# Revit family: 879-105X99-001-DN50-600
name_source: partatom
category: Pipe Accessories
units: mm (PartAtom-declared; Revit-internal decimal feet)

## family parameters
Always vertical = Yes
Cut with Voids When Loaded = No
Part Type = Valve - Breaks Into
Round Connector Dimension = Use Diameter
Shared = No
Work Plane-Based = No

## types (42) — shared parameters
879-0050-10-14400559999 = DN50_PN10/16
879-0050-10-144005599A0 = DN50_PN10/16
879-0065-10-14400559999 = DN65_PN10/16
879-0065-10-144005599A0 = DN65_PN10/16
879-0080-10-14400559999 = DN80_PN10/16
879-0080-10-144005599A0 = DN80_PN10/16
879-0100-10-14400559999 = DN100_PN10/16
879-0100-10-144005599A0 = DN100_PN10/16
879-0150-10-14400559999 = DN150_PN10/16
879-0150-10-144005599A0 = DN150_PN10/16
879-0200-10-04400559999 = DN200_PN10
879-0200-10-044005599A0 = DN200_PN10
879-0200-10-14400559999 = DN200_PN16
879-0200-10-144005599A0 = DN200_PN16
879-0250-10-04400559999 = DN250_PN10
879-0250-10-044005599A0 = DN250_PN10
879-0250-10-14400559999 = DN250_PN16
879-0250-10-144005599A0 = DN250_PN16
879-0300-10-04400559999 = DN300_PN10
879-0300-10-044005599A0 = DN300_PN10
879-0300-10-14400559999 = DN300_PN16
879-0300-10-144005599A0 = DN300_PN16
879-0350-10-04400559999 = DN350_PN10
879-0350-10-044005599A0 = DN350_PN10
879-0350-10-14400559999 = DN350_PN16
879-0350-10-144005599A0 = DN350_PN16
879-0400-10-04400559999 = DN400_PN10
879-0400-10-044005599A0 = DN400_PN10
879-0400-10-14400559999 = DN400_PN16
879-0400-10-144005599A0 = DN400_PN16
879-0450-10-04400559999 = DN450_PN10
879-0450-10-044005599A0 = DN450_PN10
879-0450-10-14400559999 = DN450_PN16
879-0450-10-144005599A0 = DN450_PN16
879-0500-10-04400559999 = DN500_PN10
879-0500-10-044005599A0 = DN500_PN10
879-0500-10-14400559999 = DN500_PN16
879-0500-10-144005599A0 = DN500_PN16
879-0600-10-04400559999 = DN600_PN10
879-0600-10-044005599A0 = DN600_PN10
879-0600-10-14400559999 = DN600_PN16
879-0600-10-144005599A0 = DN600_PN16
Body_wall_thickness = 10 mm  [stored 0.0328084 ft]
Description_ = AVK MODULATING FLOAT LEVEL CONTROL VALVE
Search_Table = 879-105X99-001-DN50-600
URL product pages = https://www.avkvalves.com

## per-type parameters (varying)
- 879-0050-10-14400559999_DN50_PN10/16: Body_Collar_Dia=18 mm; Body_Collar_Dia_2=12 mm  [stored 0.0393701 ft]; Body_Flange_Dia=61 mm; Body_Flange_Dia_2=64 mm; Body_Height_1=77 mm; Body_Height_2=29 mm; Body_Height_3=60 mm; Body_Height_4=44 mm; Body_Top_Dia=8 mm  [stored 0.0262467 ft]; Body_Top_Dia_2=6 mm  [stored 0.019685 ft]; Body_With_Dia=46 mm; Body_With_Dia_1=58 mm; Body_With_Dia_2=51 mm; Bolt_support=177 mm; Bolt_support_2=88 mm; Bolt_support_Dia=12 mm  [stored 0.0393701 ft]; Bolt_support_lenght=45 mm; Bolt_support_lenght_2=55 mm; Bottom_profile=13 mm  [stored 0.0426509 ft]; D1=50 mm; D3=83 mm; DN=50 mm; Fillet_Length=6 mm  [stored 0.019685 ft]; Fillet_Length_2=24 mm  [stored 0.0787402 ft]; Flange_thickness=19 mm  [stored 0.062336 ft]; H3=321 mm; H3_Ref=302 mm; H3_Ref_2=140 mm; ID=25 mm  [stored 0.082021 ft]; L=230 mm; PG_Dia=25 mm  [stored 0.082021 ft]; PG_Ref=51 mm; PG_depth=8 mm  [stored 0.0262467 ft]; PG_height=188 mm; PG_height_1=176 mm; PG_ref=35 mm  [stored 0.114829 ft]; PR_1=22 mm  [stored 0.0721785 ft]; P_lenght=33 mm  [stored 0.108268 ft]; Pilot_Dia_1=15 mm  [stored 0.0492126 ft]; Pilot_Dia_2=30 mm  [stored 0.0984252 ft]; Pilot_Dia_3=10 mm  [stored 0.0328084 ft]; Pilot_Dia_4=5 mm  [stored 0.0164042 ft]; Pilot_Dia_5=3 mm  [stored 0.00984252 ft]; Pilot_top_1=209 mm; Pilot_top_ref=19 mm  [stored 0.062336 ft]; Profile1_Height=100 mm; Profile1_Length=22 mm  [stored 0.0721785 ft]; Profile1_Length_2=15 mm  [stored 0.0492126 ft]; Profile_Dia=6 mm  [stored 0.019685 ft]; Profile_Dia_2=6 mm  [stored 0.019685 ft]; Profile_Dia_3=12 mm  [stored 0.0393701 ft]; Profile_height ref=41 mm  [stored 0.134514 ft]; T_Height=98 mm; T_Height_2=84 mm; T_Height_Ref_1=14 mm  [stored 0.0459318 ft]; T_Height_Ref_2=16 mm  [stored 0.0524934 ft]; Top_Profile=106 mm; Top_Profile_Ref=111 mm; W=237 mm; W_Ref=231 mm
- 879-0050-10-144005599A0_DN50_PN10/16: Body_Collar_Dia=18 mm; Body_Collar_Dia_2=12 mm  [stored 0.0393701 ft]; Body_Flange_Dia=61 mm; Body_Flange_Dia_2=64 mm; Body_Height_1=77 mm; Body_Height_2=29 mm; Body_Height_3=80 mm; Body_Height_4=44 mm; Body_Top_Dia=8 mm  [stored 0.0262467 ft]; Body_Top_Dia_2=6 mm  [stored 0.019685 ft]; Body_With_Dia=46 mm; Body_With_Dia_1=58 mm; Body_With_Dia_2=51 mm; Bolt_support=177 mm; Bolt_support_2=88 mm; Bolt_support_Dia=12 mm  [stored 0.0393701 ft]; Bolt_support_lenght=45 mm; Bolt_support_lenght_2=55 mm; Bottom_profile=13 mm  [stored 0.0426509 ft]; D1=50 mm; D3=83 mm; DN=50 mm; Fillet_Length=6 mm  [stored 0.019685 ft]; Fillet_Length_2=24 mm  [stored 0.0787402 ft]; Flange_thickness=19 mm  [stored 0.062336 ft]; H3=407 mm; H3_Ref=355 mm; H3_Ref_2=140 mm; ID=25 mm  [stored 0.082021 ft]; L=230 mm; PG_Dia=25 mm  [stored 0.082021 ft]; PG_Ref=51 mm; PG_depth=8 mm  [stored 0.0262467 ft]; PG_height=215 mm; PG_height_1=203 mm; PG_ref=35 mm  [stored 0.114829 ft]; PR_1=39 mm  [stored 0.127953 ft]; P_lenght=33 mm  [stored 0.108268 ft]; Pilot_Dia_1=15 mm  [stored 0.0492126 ft]; Pilot_Dia_2=30 mm  [stored 0.0984252 ft]; Pilot_Dia_3=10 mm  [stored 0.0328084 ft]; Pilot_Dia_4=5 mm  [stored 0.0164042 ft]; Pilot_Dia_5=3 mm  [stored 0.00984252 ft]; Pilot_top_1=262 mm; Pilot_top_ref=52 mm; Profile1_Height=110 mm; Profile1_Length=22 mm  [stored 0.0721785 ft]; Profile1_Length_2=15 mm  [stored 0.0492126 ft]; Profile_Dia=6 mm  [stored 0.019685 ft]; Profile_Dia_2=6 mm  [stored 0.019685 ft]; Profile_Dia_3=12 mm  [stored 0.0393701 ft]; Profile_height ref=41 mm  [stored 0.134514 ft]; T_Height=174 mm; T_Height_2=149 mm; T_Height_Ref_1=25 mm  [stored 0.082021 ft]; T_Height_Ref_2=29 mm; Top_Profile=106 mm; Top_Profile_Ref=111 mm; W=237 mm; W_Ref=231 mm
- 879-0065-10-14400559999_DN65_PN10/16: Body_Collar_Dia=22 mm  [stored 0.0721785 ft]; Body_Collar_Dia_2=15 mm  [stored 0.0492126 ft]; Body_Flange_Dia=76 mm; Body_Flange_Dia_2=81 mm; Body_Height_1=97 mm; Body_Height_2=36 mm  [stored 0.11811 ft]; Body_Height_3=58 mm; Body_Height_4=51 mm; Body_Top_Dia=10 mm  [stored 0.0328084 ft]; Body_Top_Dia_2=8 mm  [stored 0.0262467 ft]; Body_With_Dia=58 mm; Body_With_Dia_1=73 mm; Body_With_Dia_2=64 mm; Bolt_support=223 mm; Bolt_support_2=112 mm; Bolt_support_Dia=12 mm  [stored 0.0393701 ft]; Bolt_support_lenght=53 mm; Bolt_support_lenght_2=63 mm; Bottom_profile=16 mm  [stored 0.0524934 ft]; D1=59 mm; D3=93 mm; DN=65 mm; Fillet_Length=6 mm  [stored 0.019685 ft]; Fillet_Length_2=24 mm  [stored 0.0787402 ft]; Flange_thickness=19 mm  [stored 0.062336 ft]; H3=352 mm; H3_Ref=335 mm; H3_Ref_2=168 mm; ID=33 mm  [stored 0.108268 ft]; L=290 mm; PG_Dia=33 mm  [stored 0.108268 ft]; PG_Ref=64 mm; PG_depth=8 mm  [stored 0.0262467 ft]; PG_height=213 mm; PG_height_1=197 mm; PG_ref=43 mm; PR_1=23 mm  [stored 0.0754593 ft]; P_lenght=39 mm  [stored 0.127953 ft]; Pilot_Dia_1=18 mm; Pilot_Dia_2=35 mm  [stored 0.114829 ft]; Pilot_Dia_3=12 mm  [stored 0.0393701 ft]; Pilot_Dia_4=6 mm  [stored 0.019685 ft]; Pilot_Dia_5=4 mm  [stored 0.0131234 ft]; Pilot_top_1=233 mm; Pilot_top_ref=17 mm; Profile1_Height=117 mm; Profile1_Length=25 mm  [stored 0.082021 ft]; Profile1_Length_2=17 mm; Profile_Dia=6 mm  [stored 0.019685 ft]; Profile_Dia_2=6 mm  [stored 0.019685 ft]; Profile_Dia_3=12 mm  [stored 0.0393701 ft]; Profile_height ref=41 mm  [stored 0.134514 ft]; T_Height=102 mm; T_Height_2=87 mm; T_Height_Ref_1=15 mm  [stored 0.0492126 ft]; T_Height_Ref_2=17 mm; Top_Profile=134 mm; Top_Profile_Ref=139 mm; W=245 mm; W_Ref=239 mm
- 879-0065-10-144005599A0_DN65_PN10/16: Body_Collar_Dia=22 mm  [stored 0.0721785 ft]; Body_Collar_Dia_2=15 mm  [stored 0.0492126 ft]; Body_Flange_Dia=76 mm; Body_Flange_Dia_2=81 mm; Body_Height_1=97 mm; Body_Height_2=36 mm  [stored 0.11811 ft]; Body_Height_3=73 mm; Body_Height_4=51 mm; Body_Top_Dia=10 mm  [stored 0.0328084 ft]; Body_Top_Dia_2=8 mm  [stored 0.0262467 ft]; Body_With_Dia=58 mm; Body_With_Dia_1=73 mm; Body_With_Dia_2=64 mm; Bolt_support=223 mm; Bolt_support_2=112 mm; Bolt_support_Dia=12 mm  [stored 0.0393701 ft]; Bolt_support_lenght=53 mm; Bolt_support_lenght_2=63 mm; Bottom_profile=16 mm  [stored 0.0524934 ft]; D1=59 mm; D3=93 mm; DN=65 mm; Fillet_Length=6 mm  [stored 0.019685 ft]; Fillet_Length_2=24 mm  [stored 0.0787402 ft]; Flange_thickness=19 mm  [stored 0.062336 ft]; H3=436 mm; H3_Ref=384 mm; H3_Ref_2=168 mm; ID=33 mm  [stored 0.108268 ft]; L=290 mm; PG_Dia=33 mm  [stored 0.108268 ft]; PG_Ref=64 mm; PG_depth=8 mm  [stored 0.0262467 ft]; PG_height=246 mm; PG_height_1=230 mm; PG_ref=43 mm; PR_1=38 mm; P_lenght=39 mm  [stored 0.127953 ft]; Pilot_Dia_1=18 mm; Pilot_Dia_2=35 mm  [stored 0.114829 ft]; Pilot_Dia_3=12 mm  [stored 0.0393701 ft]; Pilot_Dia_4=6 mm  [stored 0.019685 ft]; Pilot_Dia_5=4 mm  [stored 0.0131234 ft]; Pilot_top_1=282 mm; Pilot_top_ref=52 mm; Profile1_Height=135 mm; Profile1_Length=25 mm  [stored 0.082021 ft]; Profile1_Length_2=17 mm; Profile_Dia=6 mm  [stored 0.019685 ft]; Profile_Dia_2=6 mm  [stored 0.019685 ft]; Profile_Dia_3=12 mm  [stored 0.0393701 ft]; Profile_height ref=41 mm  [stored 0.134514 ft]; T_Height=168 mm; T_Height_2=144 mm; T_Height_Ref_1=24 mm  [stored 0.0787402 ft]; T_Height_Ref_2=28 mm  [stored 0.0918635 ft]; Top_Profile=134 mm; Top_Profile_Ref=139 mm; W=245 mm; W_Ref=239 mm
- 879-0080-10-14400559999_DN80_PN10/16: Body_Collar_Dia=24 mm  [stored 0.0787402 ft]; Body_Collar_Dia_2=16 mm  [stored 0.0524934 ft]; Body_Flange_Dia=82 mm; Body_Flange_Dia_2=86 mm; Body_Height_1=103 mm; Body_Height_2=39 mm  [stored 0.127953 ft]; Body_Height_3=62 mm; Body_Height_4=54 mm; Body_Top_Dia=10 mm  [stored 0.0328084 ft]; Body_Top_Dia_2=9 mm  [stored 0.0295276 ft]; Body_With_Dia=62 mm; Body_With_Dia_1=78 mm; Body_With_Dia_2=69 mm; Bolt_support=238 mm; Bolt_support_2=119 mm; Bolt_support_Dia=12 mm  [stored 0.0393701 ft]; Bolt_support_lenght=60 mm; Bolt_support_lenght_2=70 mm; Bottom_profile=20 mm  [stored 0.0656168 ft]; D1=66 mm; D3=100 mm; DN=80 mm; Fillet_Length=6 mm  [stored 0.019685 ft]; Fillet_Length_2=24 mm  [stored 0.0787402 ft]; Flange_thickness=19 mm  [stored 0.062336 ft]; H3=367 mm; H3_Ref=353 mm; H3_Ref_2=177 mm; ID=40 mm  [stored 0.131234 ft]; L=310 mm; PG_Dia=40 mm  [stored 0.131234 ft]; PG_Ref=69 mm; PG_depth=8 mm  [stored 0.0262467 ft]; PG_height=244 mm; PG_height_1=224 mm; PG_ref=50 mm; PR_1=19 mm  [stored 0.062336 ft]; P_lenght=43 mm; Pilot_Dia_1=20 mm  [stored 0.0656168 ft]; Pilot_Dia_2=39 mm  [stored 0.127953 ft]; Pilot_Dia_3=13 mm  [stored 0.0426509 ft]; Pilot_Dia_4=7 mm  [stored 0.0229659 ft]; Pilot_Dia_5=4 mm  [stored 0.0131234 ft]; Pilot_top_1=243 mm; Pilot_top_ref=14 mm  [stored 0.0459318 ft]; Profile1_Height=144 mm; Profile1_Length=27 mm; Profile1_Length_2=18 mm; Profile_Dia=6 mm  [stored 0.019685 ft]; Profile_Dia_2=6 mm  [stored 0.019685 ft]; Profile_Dia_3=12 mm  [stored 0.0393701 ft]; Profile_height ref=41 mm  [stored 0.134514 ft]; T_Height=82 mm; T_Height_2=70 mm; T_Height_Ref_1=12 mm  [stored 0.0393701 ft]; T_Height_Ref_2=14 mm  [stored 0.0459318 ft]; Top_Profile=143 mm; Top_Profile_Ref=148 mm; W=260 mm; W_Ref=254 mm
- 879-0080-10-144005599A0_DN80_PN10/16: Body_Collar_Dia=24 mm  [stored 0.0787402 ft]; Body_Collar_Dia_2=16 mm  [stored 0.0524934 ft]; Body_Flange_Dia=82 mm; Body_Flange_Dia_2=86 mm; Body_Height_1=103 mm; Body_Height_2=39 mm  [stored 0.127953 ft]; Body_Height_3=100 mm; Body_Height_4=54 mm; Body_Top_Dia=10 mm  [stored 0.0328084 ft]; Body_Top_Dia_2=9 mm  [stored 0.0295276 ft]; Body_With_Dia=62 mm; Body_With_Dia_1=78 mm; Body_With_Dia_2=69 mm; Bolt_support=238 mm; Bolt_support_2=119 mm; Bolt_support_Dia=12 mm  [stored 0.0393701 ft]; Bolt_support_lenght=60 mm; Bolt_support_lenght_2=70 mm; Bottom_profile=20 mm  [stored 0.0656168 ft]; D1=66 mm; D3=100 mm; DN=80 mm; Fillet_Length=6 mm  [stored 0.019685 ft]; Fillet_Length_2=24 mm  [stored 0.0787402 ft]; Flange_thickness=19 mm  [stored 0.062336 ft]; H3=451 mm; H3_Ref=414 mm; H3_Ref_2=177 mm; ID=40 mm  [stored 0.131234 ft]; L=310 mm; PG_Dia=40 mm  [stored 0.131234 ft]; PG_Ref=69 mm; PG_depth=8 mm  [stored 0.0262467 ft]; PG_height=254 mm; PG_height_1=234 mm; PG_ref=50 mm; PR_1=40 mm  [stored 0.131234 ft]; P_lenght=43 mm; Pilot_Dia_1=20 mm  [stored 0.0656168 ft]; Pilot_Dia_2=39 mm  [stored 0.127953 ft]; Pilot_Dia_3=13 mm  [stored 0.0426509 ft]; Pilot_Dia_4=7 mm  [stored 0.0229659 ft]; Pilot_Dia_5=4 mm  [stored 0.0131234 ft]; Pilot_top_1=304 mm; Pilot_top_ref=37 mm; Profile1_Height=133 mm; Profile1_Length=27 mm; Profile1_Length_2=18 mm; Profile_Dia=6 mm  [stored 0.019685 ft]; Profile_Dia_2=6 mm  [stored 0.019685 ft]; Profile_Dia_3=12 mm  [stored 0.0393701 ft]; Profile_height ref=41 mm  [stored 0.134514 ft]; T_Height=177 mm; T_Height_2=152 mm; T_Height_Ref_1=25 mm  [stored 0.082021 ft]; T_Height_Ref_2=30 mm  [stored 0.0984252 ft]; Top_Profile=143 mm; Top_Profile_Ref=148 mm; W=260 mm; W_Ref=254 mm
- 879-0100-10-14400559999_DN100_PN10/16: Body_Collar_Dia=27 mm; Body_Collar_Dia_2=18 mm; Body_Flange_Dia=92 mm; Body_Flange_Dia_2=97 mm; Body_Height_1=117 mm; Body_Height_2=44 mm; Body_Height_3=50 mm; Body_Height_4=59 mm; Body_Top_Dia=12 mm  [stored 0.0393701 ft]; Body_Top_Dia_2=10 mm  [stored 0.0328084 ft]; Body_With_Dia=70 mm; Body_With_Dia_1=88 mm; Body_With_Dia_2=78 mm; Bolt_support=269 mm; Bolt_support_2=135 mm; Bolt_support_Dia=12 mm  [stored 0.0393701 ft]; Bolt_support_lenght=70 mm; Bolt_support_lenght_2=80 mm; Bottom_profile=25 mm  [stored 0.082021 ft]; D1=78 mm; D3=110 mm; DN=100 mm; Fillet_Length=6 mm  [stored 0.019685 ft]; Fillet_Length_2=24 mm  [stored 0.0787402 ft]; Flange_thickness=19 mm  [stored 0.062336 ft]; H3=390 mm; H3_Ref=373 mm; H3_Ref_2=195 mm; ID=50 mm; L=350 mm; PG_Dia=50 mm; PG_Ref=78 mm; PG_depth=8 mm  [stored 0.0262467 ft]; PG_height=261 mm; PG_height_1=236 mm; PG_ref=60 mm; PR_1=20 mm  [stored 0.0656168 ft]; P_lenght=48 mm; Pilot_Dia_1=22 mm  [stored 0.0721785 ft]; Pilot_Dia_2=44 mm; Pilot_Dia_3=15 mm  [stored 0.0492126 ft]; Pilot_Dia_4=7 mm  [stored 0.0229659 ft]; Pilot_Dia_5=5 mm  [stored 0.0164042 ft]; Pilot_top_1=253 mm; Pilot_top_ref=17 mm; Profile1_Height=150 mm; Profile1_Length=30 mm  [stored 0.0984252 ft]; Profile1_Length_2=20 mm  [stored 0.0656168 ft]; Profile_Dia=6 mm  [stored 0.019685 ft]; Profile_Dia_2=6 mm  [stored 0.019685 ft]; Profile_Dia_3=12 mm  [stored 0.0393701 ft]; Profile_height ref=41 mm  [stored 0.134514 ft]; T_Height=89 mm; T_Height_2=76 mm; T_Height_Ref_1=13 mm  [stored 0.0426509 ft]; T_Height_Ref_2=15 mm  [stored 0.0492126 ft]; Top_Profile=162 mm; Top_Profile_Ref=167 mm; W=280 mm; W_Ref=274 mm
- 879-0100-10-144005599A0_DN100_PN10/16: Body_Collar_Dia=27 mm; Body_Collar_Dia_2=18 mm; Body_Flange_Dia=92 mm; Body_Flange_Dia_2=97 mm; Body_Height_1=117 mm; Body_Height_2=44 mm; Body_Height_3=95 mm; Body_Height_4=59 mm; Body_Top_Dia=12 mm  [stored 0.0393701 ft]; Body_Top_Dia_2=10 mm  [stored 0.0328084 ft]; Body_With_Dia=70 mm; Body_With_Dia_1=88 mm; Body_With_Dia_2=78 mm; Bolt_support=269 mm; Bolt_support_2=135 mm; Bolt_support_Dia=12 mm  [stored 0.0393701 ft]; Bolt_support_lenght=70 mm; Bolt_support_lenght_2=80 mm; Bottom_profile=25 mm  [stored 0.082021 ft]; D1=78 mm; D3=110 mm; DN=100 mm; Fillet_Length=6 mm  [stored 0.019685 ft]; Fillet_Length_2=24 mm  [stored 0.0787402 ft]; Flange_thickness=19 mm  [stored 0.062336 ft]; H3=474 mm; H3_Ref=437 mm; H3_Ref_2=195 mm; ID=50 mm; L=350 mm; PG_Dia=50 mm; PG_Ref=78 mm; PG_depth=8 mm  [stored 0.0262467 ft]; PG_height=273 mm; PG_height_1=248 mm; PG_ref=60 mm; PR_1=41 mm  [stored 0.134514 ft]; P_lenght=48 mm; Pilot_Dia_1=22 mm  [stored 0.0721785 ft]; Pilot_Dia_2=44 mm; Pilot_Dia_3=15 mm  [stored 0.0492126 ft]; Pilot_Dia_4=7 mm  [stored 0.0229659 ft]; Pilot_Dia_5=5 mm  [stored 0.0164042 ft]; Pilot_top_1=317 mm; Pilot_top_ref=37 mm; Profile1_Height=141 mm; Profile1_Length=30 mm  [stored 0.0984252 ft]; Profile1_Length_2=20 mm  [stored 0.0656168 ft]; Profile_Dia=6 mm  [stored 0.019685 ft]; Profile_Dia_2=6 mm  [stored 0.019685 ft]; Profile_Dia_3=12 mm  [stored 0.0393701 ft]; Profile_height ref=41 mm  [stored 0.134514 ft]; T_Height=182 mm; T_Height_2=156 mm; T_Height_Ref_1=26 mm; T_Height_Ref_2=30 mm  [stored 0.0984252 ft]; Top_Profile=162 mm; Top_Profile_Ref=167 mm; W=280 mm; W_Ref=274 mm
- 879-0150-10-14400559999_DN150_PN10/16: Body_Collar_Dia=37 mm; Body_Collar_Dia_2=24 mm  [stored 0.0787402 ft]; Body_Flange_Dia=126 mm; Body_Flange_Dia_2=133 mm; Body_Height_1=160 mm; Body_Height_2=60 mm; Body_Height_3=60 mm; Body_Height_4=75 mm; Body_Top_Dia=16 mm  [stored 0.0524934 ft]; Body_Top_Dia_2=13 mm  [stored 0.0426509 ft]; Body_With_Dia=96 mm; Body_With_Dia_1=120 mm; Body_With_Dia_2=107 mm; Bolt_support=369 mm; Bolt_support_2=185 mm; Bolt_support_Dia=16 mm  [stored 0.0524934 ft]; Bolt_support_lenght=95 mm; Bolt_support_lenght_2=105 mm; Bottom_profile=38 mm; D1=106 mm; D3=143 mm; DN=150 mm; Fillet_Length=8 mm  [stored 0.0262467 ft]; Fillet_Length_2=32 mm  [stored 0.104987 ft]; Flange_thickness=19 mm  [stored 0.062336 ft]; H3=523 mm; H3_Ref=490 mm; H3_Ref_2=255 mm; ID=75 mm; L=480 mm; PG_Dia=50 mm; PG_Ref=107 mm; PG_depth=11 mm; PG_height=320 mm; PG_height_1=295 mm; PG_ref=85 mm; PR_1=32 mm  [stored 0.104987 ft]; P_lenght=68 mm; Pilot_Dia_1=31 mm  [stored 0.101706 ft]; Pilot_Dia_2=62 mm; Pilot_Dia_3=21 mm  [stored 0.0688976 ft]; Pilot_Dia_4=10 mm  [stored 0.0328084 ft]; Pilot_Dia_5=7 mm  [stored 0.0229659 ft]; Pilot_top_1=338 mm; Pilot_top_ref=33 mm  [stored 0.108268 ft]; Profile1_Height=195 mm; Profile1_Length=39 mm  [stored 0.127953 ft]; Profile1_Length_2=26 mm; Profile_Dia=8 mm  [stored 0.0262467 ft]; Profile_Dia_2=8 mm  [stored 0.0262467 ft]; Profile_Dia_3=16 mm  [stored 0.0524934 ft]; Profile_height ref=43 mm; T_Height=143 mm; T_Height_2=122 mm; T_Height_Ref_1=20 mm  [stored 0.0656168 ft]; T_Height_Ref_2=24 mm  [stored 0.0787402 ft]; Top_Profile=222 mm; Top_Profile_Ref=227 mm; W=410 mm; W_Ref=402 mm
- 879-0150-10-144005599A0_DN150_PN10/16: Body_Collar_Dia=37 mm; Body_Collar_Dia_2=24 mm  [stored 0.0787402 ft]; Body_Flange_Dia=126 mm; Body_Flange_Dia_2=133 mm; Body_Height_1=160 mm; Body_Height_2=60 mm; Body_Height_3=115 mm; Body_Height_4=75 mm; Body_Top_Dia=16 mm  [stored 0.0524934 ft]; Body_Top_Dia_2=13 mm  [stored 0.0426509 ft]; Body_With_Dia=96 mm; Body_With_Dia_1=120 mm; Body_With_Dia_2=107 mm; Bolt_support=369 mm; Bolt_support_2=185 mm; Bolt_support_Dia=16 mm  [stored 0.0524934 ft]; Bolt_support_lenght=95 mm; Bolt_support_lenght_2=105 mm; Bottom_profile=38 mm; D1=106 mm; D3=143 mm; DN=150 mm; Fillet_Length=8 mm  [stored 0.0262467 ft]; Fillet_Length_2=32 mm  [stored 0.104987 ft]; Flange_thickness=19 mm  [stored 0.062336 ft]; H3=607 mm; H3_Ref=560 mm; H3_Ref_2=255 mm; ID=75 mm; L=480 mm; PG_Dia=50 mm; PG_Ref=107 mm; PG_depth=11 mm; PG_height=339 mm; PG_height_1=314 mm; PG_ref=85 mm; PR_1=51 mm; P_lenght=68 mm; Pilot_Dia_1=31 mm  [stored 0.101706 ft]; Pilot_Dia_2=62 mm; Pilot_Dia_3=21 mm  [stored 0.0688976 ft]; Pilot_Dia_4=10 mm  [stored 0.0328084 ft]; Pilot_Dia_5=7 mm  [stored 0.0229659 ft]; Pilot_top_1=407 mm; Pilot_top_ref=47 mm; Profile1_Height=195 mm; Profile1_Length=39 mm  [stored 0.127953 ft]; Profile1_Length_2=26 mm; Profile_Dia=8 mm  [stored 0.0262467 ft]; Profile_Dia_2=8 mm  [stored 0.0262467 ft]; Profile_Dia_3=16 mm  [stored 0.0524934 ft]; Profile_height ref=43 mm; T_Height=227 mm; T_Height_2=194 mm; T_Height_Ref_1=32 mm  [stored 0.104987 ft]; T_Height_Ref_2=38 mm; Top_Profile=222 mm; Top_Profile_Ref=227 mm; W=410 mm; W_Ref=402 mm
- 879-0200-10-04400559999_DN200_PN10: Body_Collar_Dia=46 mm; Body_Collar_Dia_2=30 mm  [stored 0.0984252 ft]; Body_Flange_Dia=158 mm; Body_Flange_Dia_2=167 mm; Body_Height_1=200 mm; Body_Height_2=75 mm; Body_Height_3=100 mm; Body_Height_4=90 mm; Body_Top_Dia=20 mm  [stored 0.0656168 ft]; Body_Top_Dia_2=17 mm; Body_With_Dia=120 mm; Body_With_Dia_1=150 mm; Body_With_Dia_2=133 mm; Bolt_support=462 mm; Bolt_support_2=231 mm; Bolt_support_Dia=20 mm  [stored 0.0656168 ft]; Bolt_support_lenght=120 mm; Bolt_support_lenght_2=130 mm; Bottom_profile=50 mm; D1=133 mm; D3=170 mm; DN=200 mm; Fillet_Length=10 mm  [stored 0.0328084 ft]; Fillet_Length_2=40 mm  [stored 0.131234 ft]; Flange_thickness=20 mm  [stored 0.0656168 ft]; H3=677 mm; H3_Ref=629 mm; H3_Ref_2=310 mm; ID=100 mm; L=600 mm; PG_Dia=67 mm; PG_Ref=133 mm; PG_depth=14 mm  [stored 0.0459318 ft]; PG_height=400 mm; PG_height_1=367 mm; PG_ref=110 mm; PR_1=51 mm; P_lenght=85 mm; Pilot_Dia_1=39 mm  [stored 0.127953 ft]; Pilot_Dia_2=77 mm; Pilot_Dia_3=26 mm; Pilot_Dia_4=13 mm  [stored 0.0426509 ft]; Pilot_Dia_5=9 mm  [stored 0.0295276 ft]; Pilot_top_1=449 mm; Pilot_top_ref=49 mm; Profile1_Height=238 mm; Profile1_Length=46 mm; Profile1_Length_2=31 mm  [stored 0.101706 ft]; Profile_Dia=10 mm  [stored 0.0328084 ft]; Profile_Dia_2=10 mm  [stored 0.0328084 ft]; Profile_Dia_3=20 mm  [stored 0.0656168 ft]; Profile_height ref=45 mm; T_Height=224 mm; T_Height_2=192 mm; T_Height_Ref_1=32 mm  [stored 0.104987 ft]; T_Height_Ref_2=37 mm; Top_Profile=277 mm; Top_Profile_Ref=282 mm; W=510 mm; W_Ref=500 mm
- 879-0200-10-044005599A0_DN200_PN10: Body_Collar_Dia=46 mm; Body_Collar_Dia_2=30 mm  [stored 0.0984252 ft]; Body_Flange_Dia=158 mm; Body_Flange_Dia_2=167 mm; Body_Height_1=200 mm; Body_Height_2=75 mm; Body_Height_3=170 mm; Body_Height_4=90 mm; Body_Top_Dia=20 mm  [stored 0.0656168 ft]; Body_Top_Dia_2=17 mm; Body_With_Dia=120 mm; Body_With_Dia_1=150 mm; Body_With_Dia_2=133 mm; Bolt_support=462 mm; Bolt_support_2=231 mm; Bolt_support_Dia=20 mm  [stored 0.0656168 ft]; Bolt_support_lenght=120 mm; Bolt_support_lenght_2=130 mm; Bottom_profile=50 mm; D1=133 mm; D3=170 mm; DN=200 mm; Fillet_Length=10 mm  [stored 0.0328084 ft]; Fillet_Length_2=40 mm  [stored 0.131234 ft]; Flange_thickness=20 mm  [stored 0.0656168 ft]; H3=774 mm; H3_Ref=712 mm; H3_Ref_2=310 mm; ID=100 mm; L=600 mm; PG_Dia=67 mm; PG_Ref=133 mm; PG_depth=14 mm  [stored 0.0459318 ft]; PG_height=424 mm; PG_height_1=391 mm; PG_ref=110 mm; PR_1=72 mm; P_lenght=85 mm; Pilot_Dia_1=39 mm  [stored 0.127953 ft]; Pilot_Dia_2=77 mm; Pilot_Dia_3=26 mm; Pilot_Dia_4=13 mm  [stored 0.0426509 ft]; Pilot_Dia_5=9 mm  [stored 0.0295276 ft]; Pilot_top_1=532 mm; Pilot_top_ref=62 mm; Profile1_Height=240 mm; Profile1_Length=46 mm; Profile1_Length_2=31 mm  [stored 0.101706 ft]; Profile_Dia=10 mm  [stored 0.0328084 ft]; Profile_Dia_2=10 mm  [stored 0.0328084 ft]; Profile_Dia_3=20 mm  [stored 0.0656168 ft]; Profile_height ref=45 mm; T_Height=319 mm; T_Height_2=273 mm; T_Height_Ref_1=46 mm; T_Height_Ref_2=53 mm; Top_Profile=277 mm; Top_Profile_Ref=282 mm; W=510 mm; W_Ref=500 mm
- 879-0200-10-14400559999_DN200_PN16: Body_Collar_Dia=46 mm; Body_Collar_Dia_2=30 mm  [stored 0.0984252 ft]; Body_Flange_Dia=158 mm; Body_Flange_Dia_2=167 mm; Body_Height_1=200 mm; Body_Height_2=75 mm; Body_Height_3=100 mm; Body_Height_4=90 mm; Body_Top_Dia=20 mm  [stored 0.0656168 ft]; Body_Top_Dia_2=17 mm; Body_With_Dia=120 mm; Body_With_Dia_1=150 mm; Body_With_Dia_2=133 mm; Bolt_support=462 mm; Bolt_support_2=231 mm; Bolt_support_Dia=20 mm  [stored 0.0656168 ft]; Bolt_support_lenght=120 mm; Bolt_support_lenght_2=130 mm; Bottom_profile=50 mm; D1=133 mm; D3=170 mm; DN=200 mm; Fillet_Length=10 mm  [stored 0.0328084 ft]; Fillet_Length_2=40 mm  [stored 0.131234 ft]; Flange_thickness=20 mm  [stored 0.0656168 ft]; H3=677 mm; H3_Ref=629 mm; H3_Ref_2=310 mm; ID=100 mm; L=600 mm; PG_Dia=67 mm; PG_Ref=133 mm; PG_depth=14 mm  [stored 0.0459318 ft]; PG_height=400 mm; PG_height_1=367 mm; PG_ref=110 mm; PR_1=51 mm; P_lenght=85 mm; Pilot_Dia_1=39 mm  [stored 0.127953 ft]; Pilot_Dia_2=77 mm; Pilot_Dia_3=26 mm; Pilot_Dia_4=13 mm  [stored 0.0426509 ft]; Pilot_Dia_5=9 mm  [stored 0.0295276 ft]; Pilot_top_1=449 mm; Pilot_top_ref=49 mm; Profile1_Height=238 mm; Profile1_Length=46 mm; Profile1_Length_2=31 mm  [stored 0.101706 ft]; Profile_Dia=10 mm  [stored 0.0328084 ft]; Profile_Dia_2=10 mm  [stored 0.0328084 ft]; Profile_Dia_3=20 mm  [stored 0.0656168 ft]; Profile_height ref=45 mm; T_Height=224 mm; T_Height_2=192 mm; T_Height_Ref_1=32 mm  [stored 0.104987 ft]; T_Height_Ref_2=37 mm; Top_Profile=277 mm; Top_Profile_Ref=282 mm; W=510 mm; W_Ref=500 mm
- 879-0200-10-144005599A0_DN200_PN16: Body_Collar_Dia=46 mm; Body_Collar_Dia_2=30 mm  [stored 0.0984252 ft]; Body_Flange_Dia=158 mm; Body_Flange_Dia_2=167 mm; Body_Height_1=200 mm; Body_Height_2=75 mm; Body_Height_3=165 mm; Body_Height_4=90 mm; Body_Top_Dia=20 mm  [stored 0.0656168 ft]; Body_Top_Dia_2=17 mm; Body_With_Dia=120 mm; Body_With_Dia_1=150 mm; Body_With_Dia_2=133 mm; Bolt_support=462 mm; Bolt_support_2=231 mm; Bolt_support_Dia=20 mm  [stored 0.0656168 ft]; Bolt_support_lenght=120 mm; Bolt_support_lenght_2=130 mm; Bottom_profile=50 mm; D1=133 mm; D3=170 mm; DN=200 mm; Fillet_Length=10 mm  [stored 0.0328084 ft]; Fillet_Length_2=40 mm  [stored 0.131234 ft]; Flange_thickness=20 mm  [stored 0.0656168 ft]; H3=774 mm; H3_Ref=710 mm; H3_Ref_2=310 mm; ID=100 mm; L=600 mm; PG_Dia=67 mm; PG_Ref=133 mm; PG_depth=14 mm  [stored 0.0459318 ft]; PG_height=424 mm; PG_height_1=391 mm; PG_ref=110 mm; PR_1=72 mm; P_lenght=85 mm; Pilot_Dia_1=39 mm  [stored 0.127953 ft]; Pilot_Dia_2=77 mm; Pilot_Dia_3=26 mm; Pilot_Dia_4=13 mm  [stored 0.0426509 ft]; Pilot_Dia_5=9 mm  [stored 0.0295276 ft]; Pilot_top_1=530 mm; Pilot_top_ref=65 mm; Profile1_Height=240 mm; Profile1_Length=46 mm; Profile1_Length_2=31 mm  [stored 0.101706 ft]; Profile_Dia=10 mm  [stored 0.0328084 ft]; Profile_Dia_2=10 mm  [stored 0.0328084 ft]; Profile_Dia_3=20 mm  [stored 0.0656168 ft]; Profile_height ref=45 mm; T_Height=319 mm; T_Height_2=273 mm; T_Height_Ref_1=46 mm; T_Height_Ref_2=53 mm; Top_Profile=277 mm; Top_Profile_Ref=282 mm; W=510 mm; W_Ref=500 mm
- 879-0250-10-04400559999_DN250_PN10: Body_Collar_Dia=56 mm; Body_Collar_Dia_2=37 mm; Body_Flange_Dia=192 mm; Body_Flange_Dia_2=203 mm; Body_Height_1=243 mm; Body_Height_2=91 mm; Body_Height_3=81 mm; Body_Height_4=106 mm; Body_Top_Dia=24 mm  [stored 0.0787402 ft]; Body_Top_Dia_2=20 mm  [stored 0.0656168 ft]; Body_With_Dia=146 mm; Body_With_Dia_1=183 mm; Body_With_Dia_2=162 mm; Bolt_support=562 mm; Bolt_support_2=281 mm; Bolt_support_Dia=20 mm  [stored 0.0656168 ft]; Bolt_support_lenght=145 mm; Bolt_support_lenght_2=155 mm; Bottom_profile=63 mm; D1=160 mm; D3=198 mm; DN=250 mm; Fillet_Length=10 mm  [stored 0.0328084 ft]; Fillet_Length_2=40 mm  [stored 0.131234 ft]; Flange_thickness=22 mm  [stored 0.0721785 ft]; H3=757 mm; H3_Ref=703 mm; H3_Ref_2=370 mm; ID=125 mm; L=730 mm; PG_Dia=83 mm; PG_Ref=162 mm; PG_depth=14 mm  [stored 0.0459318 ft]; PG_height=458 mm; PG_height_1=416 mm; PG_ref=135 mm; PR_1=54 mm; P_lenght=101 mm; Pilot_Dia_1=46 mm; Pilot_Dia_2=92 mm; Pilot_Dia_3=31 mm  [stored 0.101706 ft]; Pilot_Dia_4=15 mm  [stored 0.0492126 ft]; Pilot_Dia_5=10 mm  [stored 0.0328084 ft]; Pilot_top_1=495 mm; Pilot_top_ref=54 mm; Profile1_Height=275 mm; Profile1_Length=53 mm; Profile1_Length_2=36 mm  [stored 0.11811 ft]; Profile_Dia=10 mm  [stored 0.0328084 ft]; Profile_Dia_2=10 mm  [stored 0.0328084 ft]; Profile_Dia_3=20 mm  [stored 0.0656168 ft]; Profile_height ref=45 mm; T_Height=240 mm; T_Height_2=205 mm; T_Height_Ref_1=34 mm; T_Height_Ref_2=40 mm  [stored 0.131234 ft]; Top_Profile=337 mm; Top_Profile_Ref=342 mm; W=555 mm; W_Ref=545 mm
- 879-0250-10-044005599A0_DN250_PN10: Body_Collar_Dia=56 mm; Body_Collar_Dia_2=37 mm; Body_Flange_Dia=192 mm; Body_Flange_Dia_2=203 mm; Body_Height_1=243 mm; Body_Height_2=91 mm; Body_Height_3=160 mm; Body_Height_4=106 mm; Body_Top_Dia=24 mm  [stored 0.0787402 ft]; Body_Top_Dia_2=20 mm  [stored 0.0656168 ft]; Body_With_Dia=146 mm; Body_With_Dia_1=183 mm; Body_With_Dia_2=162 mm; Bolt_support=562 mm; Bolt_support_2=281 mm; Bolt_support_Dia=20 mm  [stored 0.0656168 ft]; Bolt_support_lenght=145 mm; Bolt_support_lenght_2=155 mm; Bottom_profile=63 mm; D1=160 mm; D3=198 mm; DN=250 mm; Fillet_Length=10 mm  [stored 0.0328084 ft]; Fillet_Length_2=40 mm  [stored 0.131234 ft]; Flange_thickness=22 mm  [stored 0.0721785 ft]; H3=854 mm; H3_Ref=791 mm; H3_Ref_2=370 mm; ID=125 mm; L=730 mm; PG_Dia=83 mm; PG_Ref=162 mm; PG_depth=14 mm  [stored 0.0459318 ft]; PG_height=495 mm; PG_height_1=453 mm; PG_ref=135 mm; PR_1=72 mm; P_lenght=101 mm; Pilot_Dia_1=46 mm; Pilot_Dia_2=92 mm; Pilot_Dia_3=31 mm  [stored 0.101706 ft]; Pilot_Dia_4=15 mm  [stored 0.0492126 ft]; Pilot_Dia_5=10 mm  [stored 0.0328084 ft]; Pilot_top_1=583 mm; Pilot_top_ref=63 mm; Profile1_Height=295 mm; Profile1_Length=53 mm; Profile1_Length_2=36 mm  [stored 0.11811 ft]; Profile_Dia=10 mm  [stored 0.0328084 ft]; Profile_Dia_2=10 mm  [stored 0.0328084 ft]; Profile_Dia_3=20 mm  [stored 0.0656168 ft]; Profile_height ref=45 mm; T_Height=317 mm; T_Height_2=271 mm; T_Height_Ref_1=45 mm; T_Height_Ref_2=53 mm; Top_Profile=337 mm; Top_Profile_Ref=342 mm; W=555 mm; W_Ref=545 mm
- 879-0250-10-14400559999_DN250_PN16: Body_Collar_Dia=56 mm; Body_Collar_Dia_2=37 mm; Body_Flange_Dia=192 mm; Body_Flange_Dia_2=203 mm; Body_Height_1=243 mm; Body_Height_2=91 mm; Body_Height_3=81 mm; Body_Height_4=106 mm; Body_Top_Dia=24 mm  [stored 0.0787402 ft]; Body_Top_Dia_2=20 mm  [stored 0.0656168 ft]; Body_With_Dia=146 mm; Body_With_Dia_1=183 mm; Body_With_Dia_2=162 mm; Bolt_support=562 mm; Bolt_support_2=281 mm; Bolt_support_Dia=20 mm  [stored 0.0656168 ft]; Bolt_support_lenght=145 mm; Bolt_support_lenght_2=155 mm; Bottom_profile=63 mm; D1=160 mm; D3=203 mm; DN=250 mm; Fillet_Length=10 mm  [stored 0.0328084 ft]; Fillet_Length_2=40 mm  [stored 0.131234 ft]; Flange_thickness=22 mm  [stored 0.0721785 ft]; H3=757 mm; H3_Ref=705 mm; H3_Ref_2=370 mm; ID=125 mm; L=730 mm; PG_Dia=83 mm; PG_Ref=162 mm; PG_depth=14 mm  [stored 0.0459318 ft]; PG_height=449 mm; PG_height_1=407 mm; PG_ref=135 mm; PR_1=55 mm; P_lenght=103 mm; Pilot_Dia_1=47 mm; Pilot_Dia_2=94 mm; Pilot_Dia_3=31 mm  [stored 0.101706 ft]; Pilot_Dia_4=16 mm  [stored 0.0524934 ft]; Pilot_Dia_5=10 mm  [stored 0.0328084 ft]; Pilot_top_1=493 mm; Pilot_top_ref=52 mm; Profile1_Height=265 mm; Profile1_Length=55 mm; Profile1_Length_2=36 mm  [stored 0.11811 ft]; Profile_Dia=10 mm  [stored 0.0328084 ft]; Profile_Dia_2=10 mm  [stored 0.0328084 ft]; Profile_Dia_3=20 mm  [stored 0.0656168 ft]; Profile_height ref=45 mm; T_Height=245 mm; T_Height_2=210 mm; T_Height_Ref_1=35 mm  [stored 0.114829 ft]; T_Height_Ref_2=41 mm  [stored 0.134514 ft]; Top_Profile=337 mm; Top_Profile_Ref=342 mm; W=555 mm; W_Ref=545 mm
- 879-0250-10-144005599A0_DN250_PN16: Body_Collar_Dia=56 mm; Body_Collar_Dia_2=37 mm; Body_Flange_Dia=192 mm; Body_Flange_Dia_2=203 mm; Body_Height_1=243 mm; Body_Height_2=91 mm; Body_Height_3=155 mm; Body_Height_4=106 mm; Body_Top_Dia=24 mm  [stored 0.0787402 ft]; Body_Top_Dia_2=20 mm  [stored 0.0656168 ft]; Body_With_Dia=146 mm; Body_With_Dia_1=183 mm; Body_With_Dia_2=162 mm; Bolt_support=562 mm; Bolt_support_2=281 mm; Bolt_support_Dia=20 mm  [stored 0.0656168 ft]; Bolt_support_lenght=145 mm; Bolt_support_lenght_2=155 mm; Bottom_profile=63 mm; D1=160 mm; D3=203 mm; DN=250 mm; Fillet_Length=10 mm  [stored 0.0328084 ft]; Fillet_Length_2=40 mm  [stored 0.131234 ft]; Flange_thickness=22 mm  [stored 0.0721785 ft]; H3=854 mm; H3_Ref=791 mm; H3_Ref_2=370 mm; ID=125 mm; L=730 mm; PG_Dia=83 mm; PG_Ref=162 mm; PG_depth=14 mm  [stored 0.0459318 ft]; PG_height=478 mm; PG_height_1=437 mm; PG_ref=135 mm; PR_1=75 mm; P_lenght=103 mm; Pilot_Dia_1=47 mm; Pilot_Dia_2=94 mm; Pilot_Dia_3=31 mm  [stored 0.101706 ft]; Pilot_Dia_4=16 mm  [stored 0.0524934 ft]; Pilot_Dia_5=10 mm  [stored 0.0328084 ft]; Pilot_top_1=578 mm; Pilot_top_ref=63 mm; Profile1_Height=275 mm; Profile1_Length=55 mm; Profile1_Length_2=36 mm  [stored 0.11811 ft]; Profile_Dia=10 mm  [stored 0.0328084 ft]; Profile_Dia_2=10 mm  [stored 0.0328084 ft]; Profile_Dia_3=20 mm  [stored 0.0656168 ft]; Profile_height ref=45 mm; T_Height=332 mm; T_Height_2=284 mm; T_Height_Ref_1=47 mm; T_Height_Ref_2=55 mm; Top_Profile=337 mm; Top_Profile_Ref=342 mm; W=555 mm; W_Ref=545 mm
- 879-0300-10-04400559999_DN300_PN10: Body_Collar_Dia=65 mm; Body_Collar_Dia_2=43 mm; Body_Flange_Dia=224 mm; Body_Flange_Dia_2=236 mm; Body_Height_1=283 mm; Body_Height_2=106 mm; Body_Height_3=95 mm; Body_Height_4=121 mm; Body_Top_Dia=28 mm  [stored 0.0918635 ft]; Body_Top_Dia_2=24 mm  [stored 0.0787402 ft]; Body_With_Dia=170 mm; Body_With_Dia_1=213 mm; Body_With_Dia_2=189 mm; Bolt_support=654 mm; Bolt_support_2=327 mm; Bolt_support_Dia=20 mm  [stored 0.0656168 ft]; Bolt_support_lenght=170 mm; Bolt_support_lenght_2=180 mm; Bottom_profile=75 mm; D1=185 mm; D3=223 mm; DN=300 mm; Fillet_Length=10 mm  [stored 0.0328084 ft]; Fillet_Length_2=40 mm  [stored 0.131234 ft]; Flange_thickness=25 mm  [stored 0.082021 ft]; H3=826 mm; H3_Ref=784 mm; H3_Ref_2=425 mm; ID=150 mm; L=850 mm; PG_Dia=100 mm; PG_Ref=189 mm; PG_depth=14 mm  [stored 0.0459318 ft]; PG_height=523 mm; PG_height_1=473 mm; PG_ref=160 mm; PR_1=53 mm; P_lenght=116 mm; Pilot_Dia_1=53 mm; Pilot_Dia_2=105 mm; Pilot_Dia_3=35 mm  [stored 0.114829 ft]; Pilot_Dia_4=18 mm; Pilot_Dia_5=12 mm  [stored 0.0393701 ft]; Pilot_top_1=551 mm; Pilot_top_ref=42 mm  [stored 0.137795 ft]; Profile1_Height=325 mm; Profile1_Length=60 mm; Profile1_Length_2=40 mm  [stored 0.131234 ft]; Profile_Dia=10 mm  [stored 0.0328084 ft]; Profile_Dia_2=10 mm  [stored 0.0328084 ft]; Profile_Dia_3=20 mm  [stored 0.0656168 ft]; Profile_height ref=45 mm; T_Height=234 mm; T_Height_2=200 mm; T_Height_Ref_1=33 mm  [stored 0.108268 ft]; T_Height_Ref_2=39 mm  [stored 0.127953 ft]; Top_Profile=392 mm; Top_Profile_Ref=397 mm; W=605 mm; W_Ref=595 mm
- 879-0300-10-044005599A0_DN300_PN10: Body_Collar_Dia=65 mm; Body_Collar_Dia_2=43 mm; Body_Flange_Dia=224 mm; Body_Flange_Dia_2=236 mm; Body_Height_1=283 mm; Body_Height_2=106 mm; Body_Height_3=140 mm; Body_Height_4=121 mm; Body_Top_Dia=28 mm  [stored 0.0918635 ft]; Body_Top_Dia_2=24 mm  [stored 0.0787402 ft]; Body_With_Dia=170 mm; Body_With_Dia_1=213 mm; Body_With_Dia_2=189 mm; Bolt_support=654 mm; Bolt_support_2=327 mm; Bolt_support_Dia=20 mm  [stored 0.0656168 ft]; Bolt_support_lenght=170 mm; Bolt_support_lenght_2=180 mm; Bottom_profile=75 mm; D1=185 mm; D3=223 mm; DN=300 mm; Fillet_Length=10 mm  [stored 0.0328084 ft]; Fillet_Length_2=40 mm  [stored 0.131234 ft]; Flange_thickness=25 mm  [stored 0.082021 ft]; H3=923 mm; H3_Ref=855 mm; H3_Ref_2=425 mm; ID=150 mm; L=850 mm; PG_Dia=100 mm; PG_Ref=189 mm; PG_depth=14 mm  [stored 0.0459318 ft]; PG_height=553 mm; PG_height_1=503 mm; PG_ref=160 mm; PR_1=72 mm; P_lenght=116 mm; Pilot_Dia_1=53 mm; Pilot_Dia_2=105 mm; Pilot_Dia_3=35 mm  [stored 0.114829 ft]; Pilot_Dia_4=18 mm; Pilot_Dia_5=12 mm  [stored 0.0393701 ft]; Pilot_top_1=623 mm; Pilot_top_ref=68 mm; Profile1_Height=335 mm; Profile1_Length=60 mm; Profile1_Length_2=40 mm  [stored 0.131234 ft]; Profile_Dia=10 mm  [stored 0.0328084 ft]; Profile_Dia_2=10 mm  [stored 0.0328084 ft]; Profile_Dia_3=20 mm  [stored 0.0656168 ft]; Profile_height ref=45 mm; T_Height=321 mm; T_Height_2=275 mm; T_Height_Ref_1=46 mm; T_Height_Ref_2=53 mm; Top_Profile=392 mm; Top_Profile_Ref=397 mm; W=605 mm; W_Ref=595 mm
- 879-0300-10-14400559999_DN300_PN16: Body_Collar_Dia=65 mm; Body_Collar_Dia_2=43 mm; Body_Flange_Dia=224 mm; Body_Flange_Dia_2=236 mm; Body_Height_1=283 mm; Body_Height_2=106 mm; Body_Height_3=95 mm; Body_Height_4=121 mm; Body_Top_Dia=28 mm  [stored 0.0918635 ft]; Body_Top_Dia_2=24 mm  [stored 0.0787402 ft]; Body_With_Dia=170 mm; Body_With_Dia_1=213 mm; Body_With_Dia_2=189 mm; Bolt_support=654 mm; Bolt_support_2=327 mm; Bolt_support_Dia=20 mm  [stored 0.0656168 ft]; Bolt_support_lenght=170 mm; Bolt_support_lenght_2=180 mm; Bottom_profile=75 mm; D1=185 mm; D3=230 mm; DN=300 mm; Fillet_Length=10 mm  [stored 0.0328084 ft]; Fillet_Length_2=40 mm  [stored 0.131234 ft]; Flange_thickness=25 mm  [stored 0.082021 ft]; H3=826 mm; H3_Ref=788 mm; H3_Ref_2=425 mm; ID=150 mm; L=850 mm; PG_Dia=100 mm; PG_Ref=189 mm; PG_depth=14 mm  [stored 0.0459318 ft]; PG_height=521 mm; PG_height_1=471 mm; PG_ref=160 mm; PR_1=51 mm; P_lenght=120 mm; Pilot_Dia_1=55 mm; Pilot_Dia_2=109 mm; Pilot_Dia_3=36 mm  [stored 0.11811 ft]; Pilot_Dia_4=18 mm; Pilot_Dia_5=12 mm  [stored 0.0393701 ft]; Pilot_top_1=548 mm; Pilot_top_ref=38 mm; Profile1_Height=325 mm; Profile1_Length=62 mm; Profile1_Length_2=41 mm  [stored 0.134514 ft]; Profile_Dia=10 mm  [stored 0.0328084 ft]; Profile_Dia_2=10 mm  [stored 0.0328084 ft]; Profile_Dia_3=20 mm  [stored 0.0656168 ft]; Profile_height ref=45 mm; T_Height=226 mm; T_Height_2=194 mm; T_Height_Ref_1=32 mm  [stored 0.104987 ft]; T_Height_Ref_2=38 mm; Top_Profile=392 mm; Top_Profile_Ref=397 mm; W=605 mm; W_Ref=595 mm
- 879-0300-10-144005599A0_DN300_PN16: Body_Collar_Dia=65 mm; Body_Collar_Dia_2=43 mm; Body_Flange_Dia=224 mm; Body_Flange_Dia_2=236 mm; Body_Height_1=283 mm; Body_Height_2=106 mm; Body_Height_3=130 mm; Body_Height_4=121 mm; Body_Top_Dia=28 mm  [stored 0.0918635 ft]; Body_Top_Dia_2=24 mm  [stored 0.0787402 ft]; Body_With_Dia=170 mm; Body_With_Dia_1=213 mm; Body_With_Dia_2=189 mm; Bolt_support=654 mm; Bolt_support_2=327 mm; Bolt_support_Dia=20 mm  [stored 0.0656168 ft]; Bolt_support_lenght=170 mm; Bolt_support_lenght_2=180 mm; Bottom_profile=75 mm; D1=185 mm; D3=230 mm; DN=300 mm; Fillet_Length=10 mm  [stored 0.0328084 ft]; Fillet_Length_2=40 mm  [stored 0.131234 ft]; Flange_thickness=25 mm  [stored 0.082021 ft]; H3=923 mm; H3_Ref=854 mm; H3_Ref_2=425 mm; ID=150 mm; L=850 mm; PG_Dia=100 mm; PG_Ref=189 mm; PG_depth=14 mm  [stored 0.0459318 ft]; PG_height=543 mm; PG_height_1=493 mm; PG_ref=160 mm; PR_1=73 mm; P_lenght=120 mm; Pilot_Dia_1=55 mm; Pilot_Dia_2=109 mm; Pilot_Dia_3=36 mm  [stored 0.11811 ft]; Pilot_Dia_4=18 mm; Pilot_Dia_5=12 mm  [stored 0.0393701 ft]; Pilot_top_1=614 mm; Pilot_top_ref=69 mm; Profile1_Height=325 mm; Profile1_Length=62 mm; Profile1_Length_2=41 mm  [stored 0.134514 ft]; Profile_Dia=10 mm  [stored 0.0328084 ft]; Profile_Dia_2=10 mm  [stored 0.0328084 ft]; Profile_Dia_3=20 mm  [stored 0.0656168 ft]; Profile_height ref=45 mm; T_Height=323 mm; T_Height_2=277 mm; T_Height_Ref_1=46 mm; T_Height_Ref_2=54 mm; Top_Profile=392 mm; Top_Profile_Ref=397 mm; W=605 mm; W_Ref=595 mm
- 879-0350-10-04400559999_DN350_PN10: Body_Collar_Dia=75 mm; Body_Collar_Dia_2=49 mm; Body_Flange_Dia=258 mm; Body_Flange_Dia_2=272 mm; Body_Height_1=327 mm; Body_Height_2=123 mm; Body_Height_3=98 mm; Body_Height_4=138 mm; Body_Top_Dia=33 mm  [stored 0.108268 ft]; Body_Top_Dia_2=27 mm; Body_With_Dia=196 mm; Body_With_Dia_1=245 mm; Body_With_Dia_2=218 mm; Bolt_support=754 mm; Bolt_support_2=377 mm; Bolt_support_Dia=30 mm  [stored 0.0984252 ft]; Bolt_support_lenght=195 mm; Bolt_support_lenght_2=205 mm; Bottom_profile=88 mm; D1=215 mm; D3=253 mm; DN=350 mm; Fillet_Length=15 mm  [stored 0.0492126 ft]; Fillet_Length_2=60 mm; Flange_thickness=27 mm; H3=958 mm; H3_Ref=896 mm; H3_Ref_2=484 mm; ID=175 mm; L=980 mm; PG_Dia=117 mm; PG_Ref=218 mm; PG_depth=21 mm  [stored 0.0688976 ft]; PG_height=597 mm; PG_height_1=539 mm; PG_ref=185 mm; PR_1=66 mm; P_lenght=133 mm; Pilot_Dia_1=61 mm; Pilot_Dia_2=121 mm; Pilot_Dia_3=40 mm  [stored 0.131234 ft]; Pilot_Dia_4=20 mm  [stored 0.0656168 ft]; Pilot_Dia_5=13 mm  [stored 0.0426509 ft]; Pilot_top_1=634 mm; Pilot_top_ref=62 mm; Profile1_Height=365 mm; Profile1_Length=68 mm; Profile1_Length_2=45 mm; Profile_Dia=15 mm  [stored 0.0492126 ft]; Profile_Dia_2=15 mm  [stored 0.0492126 ft]; Profile_Dia_3=30 mm  [stored 0.0984252 ft]; Profile_height ref=50 mm; T_Height=291 mm; T_Height_2=249 mm; T_Height_Ref_1=42 mm  [stored 0.137795 ft]; T_Height_Ref_2=48 mm; Top_Profile=452 mm; Top_Profile_Ref=457 mm; W=710 mm; W_Ref=695 mm
- 879-0350-10-044005599A0_DN350_PN10: Body_Collar_Dia=75 mm; Body_Collar_Dia_2=49 mm; Body_Flange_Dia=258 mm; Body_Flange_Dia_2=272 mm; Body_Height_1=327 mm; Body_Height_2=123 mm; Body_Height_3=155 mm; Body_Height_4=138 mm; Body_Top_Dia=33 mm  [stored 0.108268 ft]; Body_Top_Dia_2=27 mm; Body_With_Dia=196 mm; Body_With_Dia_1=245 mm; Body_With_Dia_2=218 mm; Bolt_support=754 mm; Bolt_support_2=377 mm; Bolt_support_Dia=30 mm  [stored 0.0984252 ft]; Bolt_support_lenght=195 mm; Bolt_support_lenght_2=205 mm; Bottom_profile=88 mm; D1=215 mm; D3=253 mm; DN=350 mm; Fillet_Length=15 mm  [stored 0.0492126 ft]; Fillet_Length_2=60 mm; Flange_thickness=27 mm; H3=1045 mm; H3_Ref=968 mm; H3_Ref_2=484 mm; ID=175 mm; L=980 mm; PG_Dia=117 mm; PG_Ref=218 mm; PG_depth=21 mm  [stored 0.0688976 ft]; PG_height=617 mm; PG_height_1=559 mm; PG_ref=185 mm; PR_1=85 mm; P_lenght=133 mm; Pilot_Dia_1=61 mm; Pilot_Dia_2=121 mm; Pilot_Dia_3=40 mm  [stored 0.131234 ft]; Pilot_Dia_4=20 mm  [stored 0.0656168 ft]; Pilot_Dia_5=13 mm  [stored 0.0426509 ft]; Pilot_top_1=706 mm; Pilot_top_ref=77 mm; Profile1_Height=365 mm; Profile1_Length=68 mm; Profile1_Length_2=45 mm; Profile_Dia=15 mm  [stored 0.0492126 ft]; Profile_Dia_2=15 mm  [stored 0.0492126 ft]; Profile_Dia_3=30 mm  [stored 0.0984252 ft]; Profile_height ref=50 mm; T_Height=378 mm; T_Height_2=324 mm; T_Height_Ref_1=54 mm; T_Height_Ref_2=63 mm; Top_Profile=452 mm; Top_Profile_Ref=457 mm; W=710 mm; W_Ref=695 mm
- 879-0350-10-14400559999_DN350_PN16: Body_Collar_Dia=75 mm; Body_Collar_Dia_2=49 mm; Body_Flange_Dia=258 mm; Body_Flange_Dia_2=272 mm; Body_Height_1=327 mm; Body_Height_2=123 mm; Body_Height_3=89 mm; Body_Height_4=138 mm; Body_Top_Dia=33 mm  [stored 0.108268 ft]; Body_Top_Dia_2=27 mm; Body_With_Dia=196 mm; Body_With_Dia_1=245 mm; Body_With_Dia_2=218 mm; Bolt_support=754 mm; Bolt_support_2=377 mm; Bolt_support_Dia=30 mm  [stored 0.0984252 ft]; Bolt_support_lenght=195 mm; Bolt_support_lenght_2=205 mm; Bottom_profile=88 mm; D1=215 mm; D3=260 mm; DN=350 mm; Fillet_Length=15 mm  [stored 0.0492126 ft]; Fillet_Length_2=60 mm; Flange_thickness=27 mm; H3=958 mm; H3_Ref=896 mm; H3_Ref_2=484 mm; ID=175 mm; L=980 mm; PG_Dia=117 mm; PG_Ref=218 mm; PG_depth=21 mm  [stored 0.0688976 ft]; PG_height=588 mm; PG_height_1=530 mm; PG_ref=185 mm; PR_1=66 mm; P_lenght=139 mm; Pilot_Dia_1=63 mm; Pilot_Dia_2=126 mm; Pilot_Dia_3=42 mm  [stored 0.137795 ft]; Pilot_Dia_4=21 mm  [stored 0.0688976 ft]; Pilot_Dia_5=14 mm  [stored 0.0459318 ft]; Pilot_top_1=626 mm; Pilot_top_ref=62 mm; Profile1_Height=355 mm; Profile1_Length=70 mm; Profile1_Length_2=47 mm; Profile_Dia=15 mm  [stored 0.0492126 ft]; Profile_Dia_2=15 mm  [stored 0.0492126 ft]; Profile_Dia_3=30 mm  [stored 0.0984252 ft]; Profile_height ref=50 mm; T_Height=293 mm; T_Height_2=251 mm; T_Height_Ref_1=42 mm  [stored 0.137795 ft]; T_Height_Ref_2=49 mm; Top_Profile=452 mm; Top_Profile_Ref=457 mm; W=710 mm; W_Ref=695 mm
- 879-0350-10-144005599A0_DN350_PN16: Body_Collar_Dia=75 mm; Body_Collar_Dia_2=49 mm; Body_Flange_Dia=258 mm; Body_Flange_Dia_2=272 mm; Body_Height_1=327 mm; Body_Height_2=123 mm; Body_Height_3=150 mm; Body_Height_4=138 mm; Body_Top_Dia=33 mm  [stored 0.108268 ft]; Body_Top_Dia_2=27 mm; Body_With_Dia=196 mm; Body_With_Dia_1=245 mm; Body_With_Dia_2=218 mm; Bolt_support=754 mm; Bolt_support_2=377 mm; Bolt_support_Dia=30 mm  [stored 0.0984252 ft]; Bolt_support_lenght=195 mm; Bolt_support_lenght_2=205 mm; Bottom_profile=88 mm; D1=215 mm; D3=260 mm; DN=350 mm; Fillet_Length=15 mm  [stored 0.0492126 ft]; Fillet_Length_2=60 mm; Flange_thickness=27 mm; H3=1045 mm; H3_Ref=970 mm; H3_Ref_2=484 mm; ID=175 mm; L=980 mm; PG_Dia=117 mm; PG_Ref=218 mm; PG_depth=21 mm  [stored 0.0688976 ft]; PG_height=608 mm; PG_height_1=549 mm; PG_ref=185 mm; PR_1=86 mm; P_lenght=139 mm; Pilot_Dia_1=63 mm; Pilot_Dia_2=126 mm; Pilot_Dia_3=42 mm  [stored 0.137795 ft]; Pilot_Dia_4=21 mm  [stored 0.0688976 ft]; Pilot_Dia_5=14 mm  [stored 0.0459318 ft]; Pilot_top_1=700 mm; Pilot_top_ref=75 mm; Profile1_Height=355 mm; Profile1_Length=70 mm; Profile1_Length_2=47 mm; Profile_Dia=15 mm  [stored 0.0492126 ft]; Profile_Dia_2=15 mm  [stored 0.0492126 ft]; Profile_Dia_3=30 mm  [stored 0.0984252 ft]; Profile_height ref=50 mm; T_Height=380 mm; T_Height_2=326 mm; T_Height_Ref_1=54 mm; T_Height_Ref_2=63 mm; Top_Profile=452 mm; Top_Profile_Ref=457 mm; W=710 mm; W_Ref=695 mm
- 879-0400-10-04400559999_DN400_PN10: Body_Collar_Dia=85 mm; Body_Collar_Dia_2=55 mm; Body_Flange_Dia=289 mm; Body_Flange_Dia_2=306 mm; Body_Height_1=367 mm; Body_Height_2=138 mm; Body_Height_3=110 mm; Body_Height_4=153 mm; Body_Top_Dia=37 mm; Body_Top_Dia_2=31 mm  [stored 0.101706 ft]; Body_With_Dia=220 mm; Body_With_Dia_1=275 mm; Body_With_Dia_2=244 mm; Bolt_support=846 mm; Bolt_support_2=423 mm; Bolt_support_Dia=40 mm  [stored 0.131234 ft]; Bolt_support_lenght=220 mm; Bolt_support_lenght_2=230 mm; Bottom_profile=100 mm; D1=240 mm; D3=283 mm; DN=400 mm; Fillet_Length=20 mm  [stored 0.0656168 ft]; Fillet_Length_2=80 mm; Flange_thickness=28 mm  [stored 0.0918635 ft]; H3=1020 mm; H3_Ref=976 mm; H3_Ref_2=539 mm; ID=200 mm; L=1100 mm; PG_Dia=133 mm; PG_Ref=244 mm; PG_depth=28 mm  [stored 0.0918635 ft]; PG_height=648 mm; PG_height_1=582 mm; PG_ref=210 mm; PR_1=65 mm; P_lenght=152 mm; Pilot_Dia_1=69 mm; Pilot_Dia_2=138 mm; Pilot_Dia_3=46 mm; Pilot_Dia_4=23 mm  [stored 0.0754593 ft]; Pilot_Dia_5=15 mm  [stored 0.0492126 ft]; Pilot_top_1=683 mm; Pilot_top_ref=44 mm; Profile1_Height=395 mm; Profile1_Length=76 mm; Profile1_Length_2=51 mm; Profile_Dia=20 mm  [stored 0.0656168 ft]; Profile_Dia_2=20 mm  [stored 0.0656168 ft]; Profile_Dia_3=40 mm  [stored 0.131234 ft]; Profile_height ref=55 mm; T_Height=288 mm; T_Height_2=246 mm; T_Height_Ref_1=41 mm  [stored 0.134514 ft]; T_Height_Ref_2=48 mm; Top_Profile=508 mm; Top_Profile_Ref=513 mm; W=780 mm; W_Ref=760 mm
- 879-0400-10-044005599A0_DN400_PN10: Body_Collar_Dia=85 mm; Body_Collar_Dia_2=55 mm; Body_Flange_Dia=289 mm; Body_Flange_Dia_2=306 mm; Body_Height_1=367 mm; Body_Height_2=138 mm; Body_Height_3=185 mm; Body_Height_4=153 mm; Body_Top_Dia=37 mm; Body_Top_Dia_2=31 mm  [stored 0.101706 ft]; Body_With_Dia=220 mm; Body_With_Dia_1=275 mm; Body_With_Dia_2=244 mm; Bolt_support=846 mm; Bolt_support_2=423 mm; Bolt_support_Dia=40 mm  [stored 0.131234 ft]; Bolt_support_lenght=220 mm; Bolt_support_lenght_2=230 mm; Bottom_profile=100 mm; D1=240 mm; D3=283 mm; DN=400 mm; Fillet_Length=20 mm  [stored 0.0656168 ft]; Fillet_Length_2=80 mm; Flange_thickness=28 mm  [stored 0.0918635 ft]; H3=1183 mm; H3_Ref=1095 mm; H3_Ref_2=539 mm; ID=200 mm; L=1100 mm; PG_Dia=133 mm; PG_Ref=244 mm; PG_depth=28 mm  [stored 0.0918635 ft]; PG_height=685 mm; PG_height_1=619 mm; PG_ref=210 mm; PR_1=102 mm; P_lenght=152 mm; Pilot_Dia_1=69 mm; Pilot_Dia_2=138 mm; Pilot_Dia_3=46 mm; Pilot_Dia_4=23 mm  [stored 0.0754593 ft]; Pilot_Dia_5=15 mm  [stored 0.0492126 ft]; Pilot_top_1=802 mm; Pilot_top_ref=88 mm; Profile1_Height=395 mm; Profile1_Length=76 mm; Profile1_Length_2=51 mm; Profile_Dia=20 mm  [stored 0.0656168 ft]; Profile_Dia_2=20 mm  [stored 0.0656168 ft]; Profile_Dia_3=40 mm  [stored 0.131234 ft]; Profile_height ref=55 mm; T_Height=451 mm; T_Height_2=386 mm; T_Height_Ref_1=64 mm; T_Height_Ref_2=75 mm; Top_Profile=508 mm; Top_Profile_Ref=513 mm; W=780 mm; W_Ref=760 mm
- 879-0400-10-14400559999_DN400_PN16: Body_Collar_Dia=85 mm; Body_Collar_Dia_2=55 mm; Body_Flange_Dia=289 mm; Body_Flange_Dia_2=306 mm; Body_Height_1=367 mm; Body_Height_2=138 mm; Body_Height_3=100 mm; Body_Height_4=153 mm; Body_Top_Dia=37 mm; Body_Top_Dia_2=31 mm  [stored 0.101706 ft]; Body_With_Dia=220 mm; Body_With_Dia_1=275 mm; Body_With_Dia_2=244 mm; Bolt_support=846 mm; Bolt_support_2=423 mm; Bolt_support_Dia=40 mm  [stored 0.131234 ft]; Bolt_support_lenght=220 mm; Bolt_support_lenght_2=230 mm; Bottom_profile=100 mm; D1=240 mm; D3=290 mm; DN=400 mm; Fillet_Length=20 mm  [stored 0.0656168 ft]; Fillet_Length_2=80 mm; Flange_thickness=28 mm  [stored 0.0918635 ft]; H3=1020 mm; H3_Ref=975 mm; H3_Ref_2=539 mm; ID=200 mm; L=1100 mm; PG_Dia=133 mm; PG_Ref=244 mm; PG_depth=28 mm  [stored 0.0918635 ft]; PG_height=647 mm; PG_height_1=580 mm; PG_ref=210 mm; PR_1=63 mm; P_lenght=156 mm; Pilot_Dia_1=71 mm; Pilot_Dia_2=142 mm; Pilot_Dia_3=47 mm; Pilot_Dia_4=24 mm  [stored 0.0787402 ft]; Pilot_Dia_5=16 mm  [stored 0.0524934 ft]; Pilot_top_1=675 mm; Pilot_top_ref=45 mm; Profile1_Height=395 mm; Profile1_Length=78 mm; Profile1_Length_2=52 mm; Profile_Dia=20 mm  [stored 0.0656168 ft]; Profile_Dia_2=20 mm  [stored 0.0656168 ft]; Profile_Dia_3=40 mm  [stored 0.131234 ft]; Profile_height ref=55 mm; T_Height=280 mm; T_Height_2=240 mm; T_Height_Ref_1=40 mm  [stored 0.131234 ft]; T_Height_Ref_2=47 mm; Top_Profile=508 mm; Top_Profile_Ref=513 mm; W=780 mm; W_Ref=760 mm
- 879-0400-10-144005599A0_DN400_PN16: Body_Collar_Dia=85 mm; Body_Collar_Dia_2=55 mm; Body_Flange_Dia=289 mm; Body_Flange_Dia_2=306 mm; Body_Height_1=367 mm; Body_Height_2=138 mm; Body_Height_3=180 mm; Body_Height_4=153 mm; Body_Top_Dia=37 mm; Body_Top_Dia_2=31 mm  [stored 0.101706 ft]; Body_With_Dia=220 mm; Body_With_Dia_1=275 mm; Body_With_Dia_2=244 mm; Bolt_support=846 mm; Bolt_support_2=423 mm; Bolt_support_Dia=40 mm  [stored 0.131234 ft]; Bolt_support_lenght=220 mm; Bolt_support_lenght_2=230 mm; Bottom_profile=100 mm; D1=240 mm; D3=290 mm; DN=400 mm; Fillet_Length=20 mm  [stored 0.0656168 ft]; Fillet_Length_2=80 mm; Flange_thickness=28 mm  [stored 0.0918635 ft]; H3=1183 mm; H3_Ref=1096 mm; H3_Ref_2=539 mm; ID=200 mm; L=1100 mm; PG_Dia=133 mm; PG_Ref=244 mm; PG_depth=28 mm  [stored 0.0918635 ft]; PG_height=691 mm; PG_height_1=625 mm; PG_ref=210 mm; PR_1=98 mm; P_lenght=156 mm; Pilot_Dia_1=71 mm; Pilot_Dia_2=142 mm; Pilot_Dia_3=47 mm; Pilot_Dia_4=24 mm  [stored 0.0787402 ft]; Pilot_Dia_5=16 mm  [stored 0.0524934 ft]; Pilot_top_1=796 mm; Pilot_top_ref=87 mm; Profile1_Height=405 mm; Profile1_Length=78 mm; Profile1_Length_2=52 mm; Profile_Dia=20 mm  [stored 0.0656168 ft]; Profile_Dia_2=20 mm  [stored 0.0656168 ft]; Profile_Dia_3=40 mm  [stored 0.131234 ft]; Profile_height ref=55 mm; T_Height=433 mm; T_Height_2=371 mm; T_Height_Ref_1=62 mm; T_Height_Ref_2=72 mm; Top_Profile=508 mm; Top_Profile_Ref=513 mm; W=780 mm; W_Ref=760 mm
- 879-0450-10-04400559999_DN450_PN10: Body_Collar_Dia=92 mm; Body_Collar_Dia_2=60 mm; Body_Flange_Dia=316 mm; Body_Flange_Dia_2=333 mm; Body_Height_1=400 mm; Body_Height_2=150 mm; Body_Height_3=135 mm; Body_Height_4=165 mm; Body_Top_Dia=40 mm  [stored 0.131234 ft]; Body_Top_Dia_2=33 mm  [stored 0.108268 ft]; Body_With_Dia=240 mm; Body_With_Dia_1=300 mm; Body_With_Dia_2=267 mm; Bolt_support=923 mm; Bolt_support_2=462 mm; Bolt_support_Dia=40 mm  [stored 0.131234 ft]; Bolt_support_lenght=245 mm; Bolt_support_lenght_2=255 mm; Bottom_profile=113 mm; D1=265 mm; D3=308 mm; DN=450 mm; Fillet_Length=20 mm  [stored 0.0656168 ft]; Fillet_Length_2=80 mm; Flange_thickness=30 mm  [stored 0.0984252 ft]; H3=1198 mm; H3_Ref=1113 mm; H3_Ref_2=585 mm; ID=225 mm; L=1200 mm; PG_Dia=150 mm; PG_Ref=267 mm; PG_depth=28 mm  [stored 0.0918635 ft]; PG_height=738 mm; PG_height_1=663 mm; PG_ref=235 mm; PR_1=88 mm; P_lenght=166 mm; Pilot_Dia_1=76 mm; Pilot_Dia_2=151 mm; Pilot_Dia_3=50 mm; Pilot_Dia_4=25 mm  [stored 0.082021 ft]; Pilot_Dia_5=17 mm; Pilot_top_1=795 mm; Pilot_top_ref=85 mm; Profile1_Height=445 mm; Profile1_Length=83 mm; Profile1_Length_2=55 mm; Profile_Dia=20 mm  [stored 0.0656168 ft]; Profile_Dia_2=20 mm  [stored 0.0656168 ft]; Profile_Dia_3=40 mm  [stored 0.131234 ft]; Profile_height ref=55 mm; T_Height=391 mm; T_Height_2=335 mm; T_Height_Ref_1=56 mm; T_Height_Ref_2=65 mm; Top_Profile=554 mm; Top_Profile_Ref=559 mm; W=930 mm; W_Ref=910 mm
- 879-0450-10-044005599A0_DN450_PN10: Body_Collar_Dia=92 mm; Body_Collar_Dia_2=60 mm; Body_Flange_Dia=316 mm; Body_Flange_Dia_2=333 mm; Body_Height_1=400 mm; Body_Height_2=150 mm; Body_Height_3=260 mm; Body_Height_4=165 mm; Body_Top_Dia=40 mm  [stored 0.131234 ft]; Body_Top_Dia_2=33 mm  [stored 0.108268 ft]; Body_With_Dia=240 mm; Body_With_Dia_1=300 mm; Body_With_Dia_2=267 mm; Bolt_support=923 mm; Bolt_support_2=462 mm; Bolt_support_Dia=40 mm  [stored 0.131234 ft]; Bolt_support_lenght=245 mm; Bolt_support_lenght_2=255 mm; Bottom_profile=113 mm; D1=265 mm; D3=308 mm; DN=450 mm; Fillet_Length=20 mm  [stored 0.0656168 ft]; Fillet_Length_2=80 mm; Flange_thickness=30 mm  [stored 0.0984252 ft]; H3=1361 mm; H3_Ref=1257 mm; H3_Ref_2=585 mm; ID=225 mm; L=1200 mm; PG_Dia=150 mm; PG_Ref=267 mm; PG_depth=28 mm  [stored 0.0918635 ft]; PG_height=775 mm; PG_height_1=700 mm; PG_ref=235 mm; PR_1=125 mm; P_lenght=166 mm; Pilot_Dia_1=76 mm; Pilot_Dia_2=151 mm; Pilot_Dia_3=50 mm; Pilot_Dia_4=25 mm  [stored 0.082021 ft]; Pilot_Dia_5=17 mm; Pilot_top_1=939 mm; Pilot_top_ref=104 mm; Profile1_Height=445 mm; Profile1_Length=83 mm; Profile1_Length_2=55 mm; Profile_Dia=20 mm  [stored 0.0656168 ft]; Profile_Dia_2=20 mm  [stored 0.0656168 ft]; Profile_Dia_3=40 mm  [stored 0.131234 ft]; Profile_height ref=55 mm; T_Height=554 mm; T_Height_2=474 mm; T_Height_Ref_1=79 mm; T_Height_Ref_2=92 mm; Top_Profile=554 mm; Top_Profile_Ref=559 mm; W=930 mm; W_Ref=910 mm
- 879-0450-10-14400559999_DN450_PN16: Body_Collar_Dia=92 mm; Body_Collar_Dia_2=60 mm; Body_Flange_Dia=316 mm; Body_Flange_Dia_2=333 mm; Body_Height_1=400 mm; Body_Height_2=150 mm; Body_Height_3=120 mm; Body_Height_4=165 mm; Body_Top_Dia=40 mm  [stored 0.131234 ft]; Body_Top_Dia_2=33 mm  [stored 0.108268 ft]; Body_With_Dia=240 mm; Body_With_Dia_1=300 mm; Body_With_Dia_2=267 mm; Bolt_support=923 mm; Bolt_support_2=462 mm; Bolt_support_Dia=40 mm  [stored 0.131234 ft]; Bolt_support_lenght=245 mm; Bolt_support_lenght_2=255 mm; Bottom_profile=113 mm; D1=274 mm; D3=320 mm; DN=450 mm; Fillet_Length=20 mm  [stored 0.0656168 ft]; Fillet_Length_2=80 mm; Flange_thickness=30 mm  [stored 0.0984252 ft]; H3=1198 mm; H3_Ref=1112 mm; H3_Ref_2=585 mm; ID=225 mm; L=1200 mm; PG_Dia=150 mm; PG_Ref=267 mm; PG_depth=28 mm  [stored 0.0918635 ft]; PG_height=736 mm; PG_height_1=661 mm; PG_ref=235 mm; PR_1=86 mm; P_lenght=174 mm; Pilot_Dia_1=79 mm; Pilot_Dia_2=158 mm; Pilot_Dia_3=53 mm; Pilot_Dia_4=26 mm; Pilot_Dia_5=18 mm; Pilot_top_1=782 mm; Pilot_top_ref=87 mm; Profile1_Height=445 mm; Profile1_Length=86 mm; Profile1_Length_2=58 mm; Profile_Dia=20 mm  [stored 0.0656168 ft]; Profile_Dia_2=20 mm  [stored 0.0656168 ft]; Profile_Dia_3=40 mm  [stored 0.131234 ft]; Profile_height ref=55 mm; T_Height=378 mm; T_Height_2=324 mm; T_Height_Ref_1=54 mm; T_Height_Ref_2=63 mm; Top_Profile=554 mm; Top_Profile_Ref=559 mm; W=930 mm; W_Ref=910 mm
- 879-0450-10-144005599A0_DN450_PN16: Body_Collar_Dia=92 mm; Body_Collar_Dia_2=60 mm; Body_Flange_Dia=316 mm; Body_Flange_Dia_2=333 mm; Body_Height_1=400 mm; Body_Height_2=150 mm; Body_Height_3=260 mm; Body_Height_4=165 mm; Body_Top_Dia=40 mm  [stored 0.131234 ft]; Body_Top_Dia_2=33 mm  [stored 0.108268 ft]; Body_With_Dia=240 mm; Body_With_Dia_1=300 mm; Body_With_Dia_2=267 mm; Bolt_support=923 mm; Bolt_support_2=462 mm; Bolt_support_Dia=40 mm  [stored 0.131234 ft]; Bolt_support_lenght=245 mm; Bolt_support_lenght_2=255 mm; Bottom_profile=113 mm; D1=274 mm; D3=320 mm; DN=450 mm; Fillet_Length=20 mm  [stored 0.0656168 ft]; Fillet_Length_2=80 mm; Flange_thickness=30 mm  [stored 0.0984252 ft]; H3=1361 mm; H3_Ref=1263 mm; H3_Ref_2=585 mm; ID=225 mm; L=1200 mm; PG_Dia=150 mm; PG_Ref=267 mm; PG_depth=28 mm  [stored 0.0918635 ft]; PG_height=772 mm; PG_height_1=697 mm; PG_ref=235 mm; PR_1=122 mm; P_lenght=174 mm; Pilot_Dia_1=79 mm; Pilot_Dia_2=158 mm; Pilot_Dia_3=53 mm; Pilot_Dia_4=26 mm; Pilot_Dia_5=18 mm; Pilot_top_1=933 mm; Pilot_top_ref=98 mm; Profile1_Height=445 mm; Profile1_Length=86 mm; Profile1_Length_2=58 mm; Profile_Dia=20 mm  [stored 0.0656168 ft]; Profile_Dia_2=20 mm  [stored 0.0656168 ft]; Profile_Dia_3=40 mm  [stored 0.131234 ft]; Profile_height ref=55 mm; T_Height=541 mm; T_Height_2=464 mm; T_Height_Ref_1=77 mm; T_Height_Ref_2=90 mm; Top_Profile=554 mm; Top_Profile_Ref=559 mm; W=930 mm; W_Ref=910 mm
- 879-0500-10-04400559999_DN500_PN10: Body_Collar_Dia=96 mm; Body_Collar_Dia_2=63 mm; Body_Flange_Dia=329 mm; Body_Flange_Dia_2=347 mm; Body_Height_1=417 mm; Body_Height_2=156 mm; Body_Height_3=150 mm; Body_Height_4=171 mm; Body_Top_Dia=42 mm  [stored 0.137795 ft]; Body_Top_Dia_2=35 mm  [stored 0.114829 ft]; Body_With_Dia=250 mm; Body_With_Dia_1=313 mm; Body_With_Dia_2=278 mm; Bolt_support=962 mm; Bolt_support_2=481 mm; Bolt_support_Dia=50 mm; Bolt_support_lenght=270 mm; Bolt_support_lenght_2=280 mm; Bottom_profile=125 mm; D1=291 mm; D3=335 mm; DN=500 mm; Fillet_Length=25 mm  [stored 0.082021 ft]; Fillet_Length_2=100 mm; Flange_thickness=32 mm  [stored 0.104987 ft]; H3=1272 mm; H3_Ref=1182 mm; H3_Ref_2=608 mm; ID=250 mm; L=1250 mm; PG_Dia=167 mm; PG_Ref=278 mm; PG_depth=35 mm  [stored 0.114829 ft]; PG_height=773 mm; PG_height_1=690 mm; PG_ref=260 mm; PR_1=97 mm; P_lenght=183 mm; Pilot_Dia_1=83 mm; Pilot_Dia_2=166 mm; Pilot_Dia_3=55 mm; Pilot_Dia_4=28 mm  [stored 0.0918635 ft]; Pilot_Dia_5=18 mm; Pilot_top_1=837 mm; Pilot_top_ref=90 mm; Profile1_Height=450 mm; Profile1_Length=91 mm; Profile1_Length_2=60 mm; Profile_Dia=25 mm  [stored 0.082021 ft]; Profile_Dia_2=25 mm  [stored 0.082021 ft]; Profile_Dia_3=50 mm; Profile_height ref=60 mm; T_Height=427 mm; T_Height_2=366 mm; T_Height_Ref_1=61 mm; T_Height_Ref_2=71 mm; Top_Profile=577 mm; Top_Profile_Ref=582 mm; W=1020 mm; W_Ref=995 mm
- 879-0500-10-044005599A0_DN500_PN10: Body_Collar_Dia=96 mm; Body_Collar_Dia_2=63 mm; Body_Flange_Dia=329 mm; Body_Flange_Dia_2=347 mm; Body_Height_1=417 mm; Body_Height_2=156 mm; Body_Height_3=280 mm; Body_Height_4=171 mm; Body_Top_Dia=42 mm  [stored 0.137795 ft]; Body_Top_Dia_2=35 mm  [stored 0.114829 ft]; Body_With_Dia=250 mm; Body_With_Dia_1=313 mm; Body_With_Dia_2=278 mm; Bolt_support=962 mm; Bolt_support_2=481 mm; Bolt_support_Dia=50 mm; Bolt_support_lenght=270 mm; Bolt_support_lenght_2=280 mm; Bottom_profile=125 mm; D1=291 mm; D3=335 mm; DN=500 mm; Fillet_Length=25 mm  [stored 0.082021 ft]; Fillet_Length_2=100 mm; Flange_thickness=32 mm  [stored 0.104987 ft]; H3=1435 mm; H3_Ref=1329 mm; H3_Ref_2=608 mm; ID=250 mm; L=1250 mm; PG_Dia=167 mm; PG_Ref=278 mm; PG_depth=35 mm  [stored 0.114829 ft]; PG_height=822 mm; PG_height_1=738 mm; PG_ref=260 mm; PR_1=130 mm; P_lenght=183 mm; Pilot_Dia_1=83 mm; Pilot_Dia_2=166 mm; Pilot_Dia_3=55 mm; Pilot_Dia_4=28 mm  [stored 0.0918635 ft]; Pilot_Dia_5=18 mm; Pilot_top_1=984 mm; Pilot_top_ref=106 mm; Profile1_Height=465 mm; Profile1_Length=91 mm; Profile1_Length_2=60 mm; Profile_Dia=25 mm  [stored 0.082021 ft]; Profile_Dia_2=25 mm  [stored 0.082021 ft]; Profile_Dia_3=50 mm; Profile_height ref=60 mm; T_Height=575 mm; T_Height_2=493 mm; T_Height_Ref_1=82 mm; T_Height_Ref_2=96 mm; Top_Profile=577 mm; Top_Profile_Ref=582 mm; W=1020 mm; W_Ref=995 mm
- 879-0500-10-14400559999_DN500_PN16: Body_Collar_Dia=96 mm; Body_Collar_Dia_2=63 mm; Body_Flange_Dia=329 mm; Body_Flange_Dia_2=347 mm; Body_Height_1=417 mm; Body_Height_2=156 mm; Body_Height_3=150 mm; Body_Height_4=171 mm; Body_Top_Dia=42 mm  [stored 0.137795 ft]; Body_Top_Dia_2=35 mm  [stored 0.114829 ft]; Body_With_Dia=250 mm; Body_With_Dia_1=313 mm; Body_With_Dia_2=278 mm; Bolt_support=962 mm; Bolt_support_2=481 mm; Bolt_support_Dia=50 mm; Bolt_support_lenght=270 mm; Bolt_support_lenght_2=280 mm; Bottom_profile=125 mm; D1=305 mm; D3=358 mm; DN=500 mm; Fillet_Length=25 mm  [stored 0.082021 ft]; Fillet_Length_2=100 mm; Flange_thickness=32 mm  [stored 0.104987 ft]; H3=1272 mm; H3_Ref=1194 mm; H3_Ref_2=608 mm; ID=250 mm; L=1250 mm; PG_Dia=167 mm; PG_Ref=278 mm; PG_depth=35 mm  [stored 0.114829 ft]; PG_height=772 mm; PG_height_1=689 mm; PG_ref=260 mm; PR_1=90 mm; P_lenght=196 mm; Pilot_Dia_1=89 mm; Pilot_Dia_2=178 mm; Pilot_Dia_3=59 mm; Pilot_Dia_4=30 mm  [stored 0.0984252 ft]; Pilot_Dia_5=20 mm  [stored 0.0656168 ft]; Pilot_top_1=826 mm; Pilot_top_ref=78 mm; Profile1_Height=455 mm; Profile1_Length=97 mm; Profile1_Length_2=64 mm; Profile_Dia=25 mm  [stored 0.082021 ft]; Profile_Dia_2=25 mm  [stored 0.082021 ft]; Profile_Dia_3=50 mm; Profile_height ref=60 mm; T_Height=400 mm; T_Height_2=342 mm; T_Height_Ref_1=57 mm; T_Height_Ref_2=67 mm; Top_Profile=577 mm; Top_Profile_Ref=582 mm; W=1020 mm; W_Ref=995 mm
- 879-0600-10-04400559999_DN600_PN10: Body_Collar_Dia=112 mm; Body_Collar_Dia_2=73 mm; Body_Flange_Dia=382 mm; Body_Flange_Dia_2=403 mm; Body_Height_1=483 mm; Body_Height_2=181 mm; Body_Height_3=145 mm; Body_Height_4=196 mm; Body_Top_Dia=48 mm; Body_Top_Dia_2=40 mm  [stored 0.131234 ft]; Body_With_Dia=290 mm; Body_With_Dia_1=363 mm; Body_With_Dia_2=322 mm; Bolt_support=1115 mm; Bolt_support_2=558 mm; Bolt_support_Dia=60 mm; Bolt_support_lenght=320 mm; Bolt_support_lenght_2=330 mm; Bottom_profile=150 mm; D1=341 mm; D3=390 mm; DN=600 mm; Fillet_Length=30 mm  [stored 0.0984252 ft]; Fillet_Length_2=120 mm; Flange_thickness=36 mm  [stored 0.11811 ft]; H3=1421 mm; H3_Ref=1328 mm; H3_Ref_2=700 mm; ID=300 mm; L=1450 mm; PG_Dia=200 mm; PG_Ref=322 mm; PG_depth=42 mm  [stored 0.137795 ft]; PG_height=890 mm; PG_height_1=790 mm; PG_ref=310 mm; PR_1=100 mm; P_lenght=216 mm; Pilot_Dia_1=98 mm; Pilot_Dia_2=196 mm; Pilot_Dia_3=65 mm; Pilot_Dia_4=33 mm  [stored 0.108268 ft]; Pilot_Dia_5=22 mm  [stored 0.0721785 ft]; Pilot_top_1=928 mm; Pilot_top_ref=93 mm; Profile1_Height=525 mm; Profile1_Length=105 mm; Profile1_Length_2=70 mm; Profile_Dia=30 mm  [stored 0.0984252 ft]; Profile_Dia_2=30 mm  [stored 0.0984252 ft]; Profile_Dia_3=60 mm; Profile_height ref=65 mm; T_Height=441 mm; T_Height_2=378 mm; T_Height_Ref_1=63 mm; T_Height_Ref_2=74 mm; Top_Profile=669 mm; Top_Profile_Ref=674 mm; W=1190 mm; W_Ref=1160 mm
- 879-0600-10-044005599A0_DN600_PN10: Body_Collar_Dia=112 mm; Body_Collar_Dia_2=73 mm; Body_Flange_Dia=382 mm; Body_Flange_Dia_2=403 mm; Body_Height_1=483 mm; Body_Height_2=181 mm; Body_Height_3=280 mm; Body_Height_4=196 mm; Body_Top_Dia=48 mm; Body_Top_Dia_2=40 mm  [stored 0.131234 ft]; Body_With_Dia=290 mm; Body_With_Dia_1=363 mm; Body_With_Dia_2=322 mm; Bolt_support=1115 mm; Bolt_support_2=558 mm; Bolt_support_Dia=60 mm; Bolt_support_lenght=320 mm; Bolt_support_lenght_2=330 mm; Bottom_profile=150 mm; D1=341 mm; D3=390 mm; DN=600 mm; Fillet_Length=30 mm  [stored 0.0984252 ft]; Fillet_Length_2=120 mm; Flange_thickness=36 mm  [stored 0.11811 ft]; H3=1584 mm; H3_Ref=1477 mm; H3_Ref_2=700 mm; ID=300 mm; L=1450 mm; PG_Dia=200 mm; PG_Ref=322 mm; PG_depth=42 mm  [stored 0.137795 ft]; PG_height=934 mm; PG_height_1=834 mm; PG_ref=310 mm; PR_1=134 mm; P_lenght=216 mm; Pilot_Dia_1=98 mm; Pilot_Dia_2=196 mm; Pilot_Dia_3=65 mm; Pilot_Dia_4=33 mm  [stored 0.108268 ft]; Pilot_Dia_5=22 mm  [stored 0.0721785 ft]; Pilot_top_1=1077 mm; Pilot_top_ref=107 mm; Profile1_Height=535 mm; Profile1_Length=105 mm; Profile1_Length_2=70 mm; Profile_Dia=30 mm  [stored 0.0984252 ft]; Profile_Dia_2=30 mm  [stored 0.0984252 ft]; Profile_Dia_3=60 mm; Profile_height ref=65 mm; T_Height=594 mm; T_Height_2=509 mm; T_Height_Ref_1=85 mm; T_Height_Ref_2=99 mm; Top_Profile=669 mm; Top_Profile_Ref=674 mm; W=1190 mm; W_Ref=1160 mm
- 879-0600-10-14400559999_DN600_PN16: Body_Collar_Dia=112 mm; Body_Collar_Dia_2=73 mm; Body_Flange_Dia=382 mm; Body_Flange_Dia_2=403 mm; Body_Height_1=483 mm; Body_Height_2=181 mm; Body_Height_3=145 mm; Body_Height_4=196 mm; Body_Top_Dia=48 mm; Body_Top_Dia_2=40 mm  [stored 0.131234 ft]; Body_With_Dia=290 mm; Body_With_Dia_1=363 mm; Body_With_Dia_2=322 mm; Bolt_support=1115 mm; Bolt_support_2=558 mm; Bolt_support_Dia=60 mm; Bolt_support_lenght=320 mm; Bolt_support_lenght_2=330 mm; Bottom_profile=150 mm; D1=360 mm; D3=420 mm; DN=600 mm; Fillet_Length=30 mm  [stored 0.0984252 ft]; Fillet_Length_2=120 mm; Flange_thickness=36 mm  [stored 0.11811 ft]; H3=1421 mm; H3_Ref=1343 mm; H3_Ref_2=700 mm; ID=300 mm; L=1450 mm; PG_Dia=200 mm; PG_Ref=322 mm; PG_depth=42 mm  [stored 0.137795 ft]; PG_height=887 mm; PG_height_1=787 mm; PG_ref=310 mm; PR_1=92 mm; P_lenght=233 mm; Pilot_Dia_1=106 mm; Pilot_Dia_2=212 mm; Pilot_Dia_3=71 mm; Pilot_Dia_4=35 mm  [stored 0.114829 ft]; Pilot_Dia_5=24 mm  [stored 0.0787402 ft]; Pilot_top_1=913 mm; Pilot_top_ref=78 mm; Profile1_Height=530 mm; Profile1_Length=114 mm; Profile1_Length_2=76 mm; Profile_Dia=30 mm  [stored 0.0984252 ft]; Profile_Dia_2=30 mm  [stored 0.0984252 ft]; Profile_Dia_3=60 mm; Profile_height ref=65 mm; T_Height=406 mm; T_Height_2=348 mm; T_Height_Ref_1=58 mm; T_Height_Ref_2=68 mm; Top_Profile=669 mm; Top_Profile_Ref=674 mm; W=1190 mm; W_Ref=1160 mm
- 879-0600-10-144005599A0_DN600_PN16: Body_Collar_Dia=112 mm; Body_Collar_Dia_2=73 mm; Body_Flange_Dia=382 mm; Body_Flange_Dia_2=403 mm; Body_Height_1=483 mm; Body_Height_2=181 mm; Body_Height_3=250 mm; Body_Height_4=196 mm; Body_Top_Dia=48 mm; Body_Top_Dia_2=40 mm  [stored 0.131234 ft]; Body_With_Dia=290 mm; Body_With_Dia_1=363 mm; Body_With_Dia_2=322 mm; Bolt_support=1115 mm; Bolt_support_2=558 mm; Bolt_support_Dia=60 mm; Bolt_support_lenght=320 mm; Bolt_support_lenght_2=330 mm; Bottom_profile=150 mm; D1=360 mm; D3=420 mm; DN=600 mm; Fillet_Length=30 mm  [stored 0.0984252 ft]; Fillet_Length_2=120 mm; Flange_thickness=36 mm  [stored 0.11811 ft]; H3=1584 mm; H3_Ref=1477 mm; H3_Ref_2=700 mm; ID=300 mm; L=1450 mm; PG_Dia=200 mm; PG_Ref=322 mm; PG_depth=42 mm  [stored 0.137795 ft]; PG_height=928 mm; PG_height_1=828 mm; PG_ref=310 mm; PR_1=128 mm; P_lenght=233 mm; Pilot_Dia_1=106 mm; Pilot_Dia_2=212 mm; Pilot_Dia_3=71 mm; Pilot_Dia_4=35 mm  [stored 0.114829 ft]; Pilot_Dia_5=24 mm  [stored 0.0787402 ft]; Pilot_top_1=1047 mm; Pilot_top_ref=107 mm; Profile1_Height=535 mm; Profile1_Length=114 mm; Profile1_Length_2=76 mm; Profile_Dia=30 mm  [stored 0.0984252 ft]; Profile_Dia_2=30 mm  [stored 0.0984252 ft]; Profile_Dia_3=60 mm; Profile_height ref=65 mm; T_Height=564 mm; T_Height_2=483 mm; T_Height_Ref_1=81 mm; T_Height_Ref_2=94 mm; Top_Profile=669 mm; Top_Profile_Ref=674 mm; W=1190 mm; W_Ref=1160 mm
- 879-0500-10-144005599A0_DN500_PN16: Body_Collar_Dia=96 mm; Body_Collar_Dia_2=63 mm; Body_Flange_Dia=329 mm; Body_Flange_Dia_2=347 mm; Body_Height_1=417 mm; Body_Height_2=156 mm; Body_Height_3=270 mm; Body_Height_4=171 mm; Body_Top_Dia=42 mm  [stored 0.137795 ft]; Body_Top_Dia_2=35 mm  [stored 0.114829 ft]; Body_With_Dia=250 mm; Body_With_Dia_1=313 mm; Body_With_Dia_2=278 mm; Bolt_support=962 mm; Bolt_support_2=481 mm; Bolt_support_Dia=50 mm; Bolt_support_lenght=270 mm; Bolt_support_lenght_2=280 mm; Bottom_profile=125 mm; D1=305 mm; D3=358 mm; DN=500 mm; Fillet_Length=25 mm  [stored 0.082021 ft]; Fillet_Length_2=100 mm; Flange_thickness=32 mm  [stored 0.104987 ft]; H3=1435 mm; H3_Ref=1335 mm; H3_Ref_2=608 mm; ID=250 mm; L=1250 mm; PG_Dia=167 mm; PG_Ref=278 mm; PG_depth=35 mm  [stored 0.114829 ft]; PG_height=809 mm; PG_height_1=726 mm; PG_ref=260 mm; PR_1=127 mm; P_lenght=196 mm; Pilot_Dia_1=89 mm; Pilot_Dia_2=178 mm; Pilot_Dia_3=59 mm; Pilot_Dia_4=30 mm  [stored 0.0984252 ft]; Pilot_Dia_5=20 mm  [stored 0.0656168 ft]; Pilot_top_1=968 mm; Pilot_top_ref=100 mm; Profile1_Height=455 mm; Profile1_Length=97 mm; Profile1_Length_2=64 mm; Profile_Dia=25 mm  [stored 0.082021 ft]; Profile_Dia_2=25 mm  [stored 0.082021 ft]; Profile_Dia_3=50 mm; Profile_height ref=60 mm; T_Height=563 mm; T_Height_2=482 mm; T_Height_Ref_1=80 mm; T_Height_Ref_2=94 mm; Top_Profile=577 mm; Top_Profile_Ref=582 mm; W=1020 mm; W_Ref=995 mm

note: [stored X ft] marks values corroborated as IEEE doubles in the binary element streams (Revit-internal decimal feet)

## geometry (parser evidence)
native form markers: Sweep x3
no freeform markers — native parametric forms only
